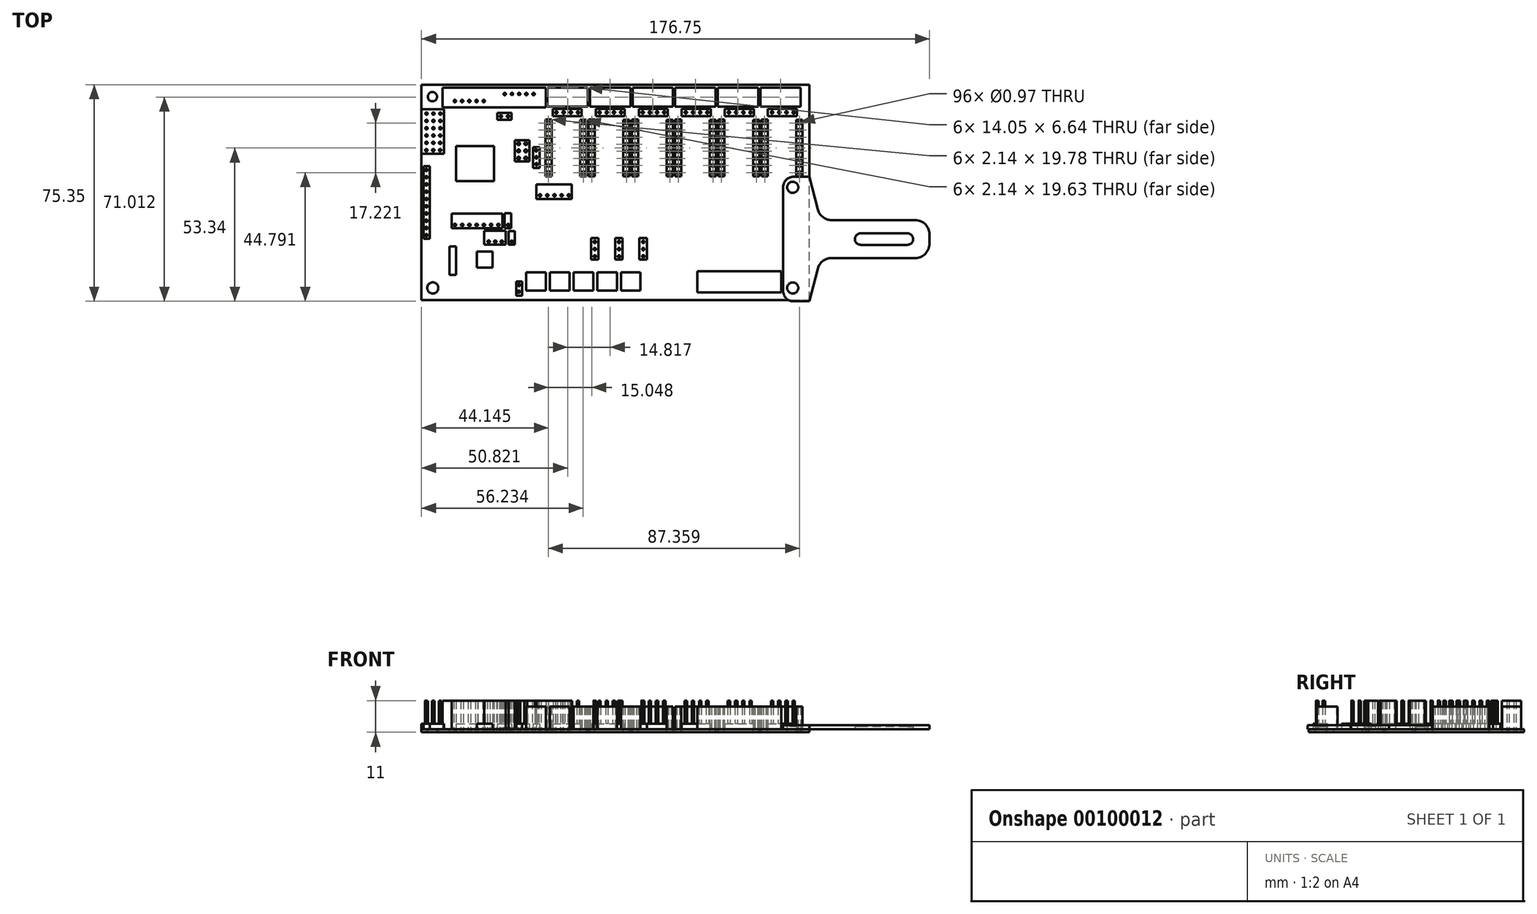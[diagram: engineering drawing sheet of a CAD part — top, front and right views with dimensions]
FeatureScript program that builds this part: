
annotation { "Feature Type Name" : "Feature", "Feature Type Description" : "" }
export const myFeature = defineFeature(function(context is Context, id is Id, definition is map)
    precondition{}
    {
        {
            var Q0;
            Q0=qCreatedBy(makeId("Top.planeOp"),FACE);
            var sketch = newSketch(context, id + "F0", { "sketchPlane" : qUnion([Q0])});
            skLineSegment(sketch, "E0", {"start": v(-38.75, 31.78) * mm, "end": v(-38.75, -41.43) * mm});
            skLineSegment(sketch, "E1", {"start": v(-38.75, -41.43) * mm, "end": v(96.25, -41.43) * mm});
            skLineSegment(sketch, "E2", {"start": v(96.25, -41.43) * mm, "end": v(96.25, 33.57) * mm});
            skLineSegment(sketch, "E3.bottom", {"start": v(-2.37, -31.77) * mm, "end": v(4.45, -31.77) * mm});
            skLineSegment(sketch, "E3.top", {"start": v(-2.37, -38.05) * mm, "end": v(4.45, -38.05) * mm});
            skLineSegment(sketch, "E3.left", {"start": v(-2.37, -31.77) * mm, "end": v(-2.37, -38.05) * mm});
            skLineSegment(sketch, "E3.right", {"start": v(4.45, -31.77) * mm, "end": v(4.45, -38.05) * mm});
            skLineSegment(sketch, "E4.1.0.0", {"start": v(12.7, -31.77) * mm, "end": v(12.7, -38.05) * mm});
            skLineSegment(sketch, "E4.1.0.1", {"start": v(5.88, -31.77) * mm, "end": v(12.7, -31.77) * mm});
            skLineSegment(sketch, "E4.1.0.2", {"start": v(5.88, -31.77) * mm, "end": v(5.88, -38.05) * mm});
            skLineSegment(sketch, "E4.1.0.3", {"start": v(5.88, -38.05) * mm, "end": v(12.7, -38.05) * mm});
            skLineSegment(sketch, "E4.2.0.0", {"start": v(20.95, -31.77) * mm, "end": v(20.95, -38.05) * mm});
            skLineSegment(sketch, "E4.2.0.1", {"start": v(14.13, -31.77) * mm, "end": v(20.95, -31.77) * mm});
            skLineSegment(sketch, "E4.2.0.2", {"start": v(14.13, -31.77) * mm, "end": v(14.13, -38.05) * mm});
            skLineSegment(sketch, "E4.2.0.3", {"start": v(14.13, -38.05) * mm, "end": v(20.95, -38.05) * mm});
            skLineSegment(sketch, "E4.3.0.0", {"start": v(29.2, -31.77) * mm, "end": v(29.2, -38.05) * mm});
            skLineSegment(sketch, "E4.3.0.1", {"start": v(22.38, -31.77) * mm, "end": v(29.2, -31.77) * mm});
            skLineSegment(sketch, "E4.3.0.2", {"start": v(22.38, -31.77) * mm, "end": v(22.38, -38.05) * mm});
            skLineSegment(sketch, "E4.3.0.3", {"start": v(22.38, -38.05) * mm, "end": v(29.2, -38.05) * mm});
            skLineSegment(sketch, "E4.4.0.0", {"start": v(37.45, -31.77) * mm, "end": v(37.45, -38.05) * mm});
            skLineSegment(sketch, "E4.4.0.1", {"start": v(30.63, -31.77) * mm, "end": v(37.45, -31.77) * mm});
            skLineSegment(sketch, "E4.4.0.2", {"start": v(30.63, -31.77) * mm, "end": v(30.63, -38.05) * mm});
            skLineSegment(sketch, "E4.4.0.3", {"start": v(30.63, -38.05) * mm, "end": v(37.45, -38.05) * mm});
            skLineSegment(sketch, "E4.direction1", {"start": v(-2.37, -38.05) * mm, "end": v(5.88, -38.05) * mm, "construction": true});
            skLineSegment(sketch, "E5", {"start": v(57.17, -31.32) * mm, "end": v(86.44, -31.32) * mm});
            skLineSegment(sketch, "E6", {"start": v(86.44, -31.32) * mm, "end": v(86.44, -38.69) * mm});
            skLineSegment(sketch, "E7", {"start": v(86.44, -38.69) * mm, "end": v(57.17, -38.69) * mm});
            skLineSegment(sketch, "E8", {"start": v(57.17, -38.69) * mm, "end": v(57.17, -31.32) * mm});
            skLineSegment(sketch, "E9.bottom", {"start": v(20.26, -19.76) * mm, "end": v(22.82, -19.76) * mm});
            skLineSegment(sketch, "E9.top", {"start": v(20.26, -27.24) * mm, "end": v(22.82, -27.24) * mm});
            skLineSegment(sketch, "E9.left", {"start": v(20.26, -19.76) * mm, "end": v(20.26, -27.24) * mm});
            skLineSegment(sketch, "E9.right", {"start": v(22.82, -19.76) * mm, "end": v(22.82, -27.24) * mm});
            skLineSegment(sketch, "E10.1.0.0", {"start": v(28.66, -19.76) * mm, "end": v(31.22, -19.76) * mm});
            skLineSegment(sketch, "E10.1.0.1", {"start": v(31.22, -19.76) * mm, "end": v(31.22, -27.24) * mm});
            skLineSegment(sketch, "E10.1.0.2", {"start": v(28.66, -19.76) * mm, "end": v(28.66, -27.24) * mm});
            skLineSegment(sketch, "E10.1.0.3", {"start": v(28.66, -27.24) * mm, "end": v(31.22, -27.24) * mm});
            skLineSegment(sketch, "E10.2.0.0", {"start": v(37.06, -19.76) * mm, "end": v(39.63, -19.76) * mm});
            skLineSegment(sketch, "E10.2.0.1", {"start": v(39.63, -19.76) * mm, "end": v(39.63, -27.24) * mm});
            skLineSegment(sketch, "E10.2.0.2", {"start": v(37.06, -19.76) * mm, "end": v(37.06, -27.24) * mm});
            skLineSegment(sketch, "E10.2.0.3", {"start": v(37.06, -27.24) * mm, "end": v(39.63, -27.24) * mm});
            skLineSegment(sketch, "E10.direction1", {"start": v(20.26, -27.24) * mm, "end": v(28.66, -27.24) * mm, "construction": true});
            skLineSegment(sketch, "E11.bottom", {"start": v(-28.27, -11.21) * mm, "end": v(-10.6, -11.21) * mm});
            skLineSegment(sketch, "E11.top", {"start": v(-28.27, -16.39) * mm, "end": v(-10.6, -16.39) * mm});
            skLineSegment(sketch, "E11.left", {"start": v(-28.27, -11.21) * mm, "end": v(-28.27, -16.39) * mm});
            skLineSegment(sketch, "E11.right", {"start": v(-10.6, -11.21) * mm, "end": v(-10.6, -16.39) * mm});
            skLineSegment(sketch, "E12.bottom", {"start": v(-17, -17.19) * mm, "end": v(-9.44, -17.19) * mm});
            skLineSegment(sketch, "E12.top", {"start": v(-17, -22.08) * mm, "end": v(-9.44, -22.08) * mm});
            skLineSegment(sketch, "E12.left", {"start": v(-17, -17.19) * mm, "end": v(-17, -22.08) * mm});
            skLineSegment(sketch, "E12.right", {"start": v(-9.44, -17.19) * mm, "end": v(-9.44, -22.08) * mm});
            skLineSegment(sketch, "E13.bottom", {"start": v(-8.45, -17.31) * mm, "end": v(-6.31, -17.31) * mm});
            skLineSegment(sketch, "E13.top", {"start": v(-8.45, -22) * mm, "end": v(-6.31, -22) * mm});
            skLineSegment(sketch, "E13.left", {"start": v(-8.45, -17.31) * mm, "end": v(-8.45, -22) * mm});
            skLineSegment(sketch, "E13.right", {"start": v(-6.31, -17.31) * mm, "end": v(-6.31, -22) * mm});
            skLineSegment(sketch, "E14.bottom", {"start": v(-5.85, -34.9) * mm, "end": v(-3.8, -34.9) * mm});
            skLineSegment(sketch, "E14.top", {"start": v(-5.85, -39.87) * mm, "end": v(-3.8, -39.87) * mm});
            skLineSegment(sketch, "E14.left", {"start": v(-5.85, -34.9) * mm, "end": v(-5.85, -39.87) * mm});
            skLineSegment(sketch, "E14.right", {"start": v(-3.8, -34.9) * mm, "end": v(-3.8, -39.87) * mm});
            skLineSegment(sketch, "E15.bottom", {"start": v(-29, -22.74) * mm, "end": v(-26.78, -22.74) * mm});
            skLineSegment(sketch, "E15.top", {"start": v(-29, -32.62) * mm, "end": v(-26.78, -32.62) * mm});
            skLineSegment(sketch, "E15.left", {"start": v(-29, -22.74) * mm, "end": v(-29, -32.62) * mm});
            skLineSegment(sketch, "E15.right", {"start": v(-26.78, -22.74) * mm, "end": v(-26.78, -32.62) * mm});
            skLineSegment(sketch, "E16.bottom", {"start": v(1.15, -1.07) * mm, "end": v(13.52, -1.07) * mm});
            skLineSegment(sketch, "E16.top", {"start": v(1.15, -6.2) * mm, "end": v(13.52, -6.2) * mm});
            skLineSegment(sketch, "E16.left", {"start": v(1.15, -1.07) * mm, "end": v(1.15, -6.2) * mm});
            skLineSegment(sketch, "E16.right", {"start": v(13.52, -1.07) * mm, "end": v(13.52, -6.2) * mm});
            skLineSegment(sketch, "E17.bottom", {"start": v(-38.08, 5.19) * mm, "end": v(-35.87, 5.19) * mm});
            skLineSegment(sketch, "E17.top", {"start": v(-38.08, -20.02) * mm, "end": v(-35.87, -20.02) * mm});
            skLineSegment(sketch, "E17.left", {"start": v(-38.08, 5.19) * mm, "end": v(-38.08, -20.02) * mm});
            skLineSegment(sketch, "E17.right", {"start": v(-35.87, 5.19) * mm, "end": v(-35.87, -20.02) * mm});
            skLineSegment(sketch, "E18.bottom", {"start": v(0.03, 11.83) * mm, "end": v(2.32, 11.83) * mm});
            skLineSegment(sketch, "E18.top", {"start": v(0.03, 4.65) * mm, "end": v(2.32, 4.65) * mm});
            skLineSegment(sketch, "E18.left", {"start": v(0.03, 11.83) * mm, "end": v(0.03, 4.65) * mm});
            skLineSegment(sketch, "E18.right", {"start": v(2.32, 11.83) * mm, "end": v(2.32, 4.65) * mm});
            skLineSegment(sketch, "E19.bottom", {"start": v(-12.42, 23.8) * mm, "end": v(-7.46, 23.8) * mm});
            skLineSegment(sketch, "E19.top", {"start": v(-12.42, 21.38) * mm, "end": v(-7.46, 21.38) * mm});
            skLineSegment(sketch, "E19.left", {"start": v(-12.42, 23.8) * mm, "end": v(-12.42, 21.38) * mm});
            skLineSegment(sketch, "E19.right", {"start": v(-7.46, 23.8) * mm, "end": v(-7.46, 21.38) * mm});
            skLineSegment(sketch, "E20.bottom", {"start": v(-26.74, 12.21) * mm, "end": v(-13.5, 12.21) * mm});
            skLineSegment(sketch, "E20.top", {"start": v(-26.74, 0.07) * mm, "end": v(-13.5, 0.07) * mm});
            skLineSegment(sketch, "E20.left", {"start": v(-26.74, 12.21) * mm, "end": v(-26.74, 0.07) * mm});
            skLineSegment(sketch, "E20.right", {"start": v(-13.5, 12.21) * mm, "end": v(-13.5, 0.07) * mm});
            skLineSegment(sketch, "E21.bottom", {"start": v(-38.75, 25.04) * mm, "end": v(-30.92, 25.04) * mm});
            skLineSegment(sketch, "E21.top", {"start": v(-38.75, 9.54) * mm, "end": v(-30.92, 9.54) * mm});
            skLineSegment(sketch, "E21.left", {"start": v(-38.75, 25.04) * mm, "end": v(-38.75, 9.54) * mm});
            skLineSegment(sketch, "E21.right", {"start": v(-30.92, 25.04) * mm, "end": v(-30.92, 9.54) * mm});
            skLineSegment(sketch, "E22", {"start": v(96.25, 33.57) * mm, "end": v(-38.75, 33.57) * mm});
            skLineSegment(sketch, "E23", {"start": v(-38.75, 33.57) * mm, "end": v(-38.75, 31.78) * mm});
            skLineSegment(sketch, "E24.bottom", {"start": v(-31.44, 32.53) * mm, "end": v(4.51, 32.53) * mm});
            skLineSegment(sketch, "E24.top", {"start": v(-31.44, 25.72) * mm, "end": v(4.51, 25.72) * mm});
            skLineSegment(sketch, "E24.left", {"start": v(-31.44, 32.53) * mm, "end": v(-31.44, 25.72) * mm});
            skLineSegment(sketch, "E24.right", {"start": v(4.51, 32.53) * mm, "end": v(4.51, 25.72) * mm});
            skLineSegment(sketch, "E25.bottom", {"start": v(5.04, 32.55) * mm, "end": v(19.1, 32.55) * mm});
            skLineSegment(sketch, "E25.top", {"start": v(5.04, 25.9) * mm, "end": v(19.1, 25.9) * mm});
            skLineSegment(sketch, "E25.left", {"start": v(5.04, 32.55) * mm, "end": v(5.04, 25.9) * mm});
            skLineSegment(sketch, "E25.right", {"start": v(19.1, 32.55) * mm, "end": v(19.1, 25.9) * mm});
            skLineSegment(sketch, "E26.1.0.0", {"start": v(33.91, 32.55) * mm, "end": v(33.91, 25.9) * mm});
            skLineSegment(sketch, "E26.1.0.1", {"start": v(19.86, 32.55) * mm, "end": v(33.91, 32.55) * mm});
            skLineSegment(sketch, "E26.1.0.2", {"start": v(19.86, 32.55) * mm, "end": v(19.86, 25.9) * mm});
            skLineSegment(sketch, "E26.1.0.3", {"start": v(19.86, 25.9) * mm, "end": v(33.91, 25.9) * mm});
            skLineSegment(sketch, "E26.2.0.0", {"start": v(48.73, 32.55) * mm, "end": v(48.73, 25.9) * mm});
            skLineSegment(sketch, "E26.2.0.1", {"start": v(34.68, 32.55) * mm, "end": v(48.73, 32.55) * mm});
            skLineSegment(sketch, "E26.2.0.2", {"start": v(34.68, 32.55) * mm, "end": v(34.68, 25.9) * mm});
            skLineSegment(sketch, "E26.2.0.3", {"start": v(34.68, 25.9) * mm, "end": v(48.73, 25.9) * mm});
            skLineSegment(sketch, "E26.3.0.0", {"start": v(63.55, 32.55) * mm, "end": v(63.55, 25.9) * mm});
            skLineSegment(sketch, "E26.3.0.1", {"start": v(49.5, 32.55) * mm, "end": v(63.55, 32.55) * mm});
            skLineSegment(sketch, "E26.3.0.2", {"start": v(49.5, 32.55) * mm, "end": v(49.5, 25.9) * mm});
            skLineSegment(sketch, "E26.3.0.3", {"start": v(49.5, 25.9) * mm, "end": v(63.55, 25.9) * mm});
            skLineSegment(sketch, "E26.4.0.0", {"start": v(78.36, 32.55) * mm, "end": v(78.36, 25.9) * mm});
            skLineSegment(sketch, "E26.4.0.1", {"start": v(64.31, 32.55) * mm, "end": v(78.36, 32.55) * mm});
            skLineSegment(sketch, "E26.4.0.2", {"start": v(64.31, 32.55) * mm, "end": v(64.31, 25.9) * mm});
            skLineSegment(sketch, "E26.4.0.3", {"start": v(64.31, 25.9) * mm, "end": v(78.36, 25.9) * mm});
            skLineSegment(sketch, "E26.5.0.0", {"start": v(93.18, 32.55) * mm, "end": v(93.18, 25.9) * mm});
            skLineSegment(sketch, "E26.5.0.1", {"start": v(79.13, 32.55) * mm, "end": v(93.18, 32.55) * mm});
            skLineSegment(sketch, "E26.5.0.2", {"start": v(79.13, 32.55) * mm, "end": v(79.13, 25.9) * mm});
            skLineSegment(sketch, "E26.5.0.3", {"start": v(79.13, 25.9) * mm, "end": v(93.18, 25.9) * mm});
            skLineSegment(sketch, "E26.direction1", {"start": v(5.04, 25.9) * mm, "end": v(19.86, 25.9) * mm, "construction": true});
            skLineSegment(sketch, "E27.bottom", {"start": v(4.33, 21.45) * mm, "end": v(6.46, 21.45) * mm});
            skLineSegment(sketch, "E27.top", {"start": v(4.33, 1.67) * mm, "end": v(6.46, 1.67) * mm});
            skLineSegment(sketch, "E27.left", {"start": v(4.33, 21.45) * mm, "end": v(4.33, 1.67) * mm});
            skLineSegment(sketch, "E27.right", {"start": v(6.46, 21.45) * mm, "end": v(6.46, 1.67) * mm});
            skLineSegment(sketch, "E28.bottom", {"start": v(16.41, 21.37) * mm, "end": v(18.55, 21.37) * mm});
            skLineSegment(sketch, "E28.top", {"start": v(16.41, 1.75) * mm, "end": v(18.55, 1.75) * mm});
            skLineSegment(sketch, "E28.left", {"start": v(16.41, 21.37) * mm, "end": v(16.41, 1.75) * mm});
            skLineSegment(sketch, "E28.right", {"start": v(18.55, 21.37) * mm, "end": v(18.55, 1.75) * mm});
            skLineSegment(sketch, "E29.1.0.0", {"start": v(19.37, 21.45) * mm, "end": v(21.51, 21.45) * mm});
            skLineSegment(sketch, "E29.1.0.1", {"start": v(21.51, 21.45) * mm, "end": v(21.51, 1.67) * mm});
            skLineSegment(sketch, "E29.1.0.2", {"start": v(19.37, 21.45) * mm, "end": v(19.37, 1.67) * mm});
            skLineSegment(sketch, "E29.1.0.3", {"start": v(19.37, 1.67) * mm, "end": v(21.51, 1.67) * mm});
            skLineSegment(sketch, "E29.1.0.4", {"start": v(31.46, 21.37) * mm, "end": v(31.46, 1.75) * mm});
            skLineSegment(sketch, "E29.1.0.5", {"start": v(31.46, 1.75) * mm, "end": v(33.6, 1.75) * mm});
            skLineSegment(sketch, "E29.1.0.6", {"start": v(33.6, 21.37) * mm, "end": v(33.6, 1.75) * mm});
            skLineSegment(sketch, "E29.1.0.7", {"start": v(31.46, 21.37) * mm, "end": v(33.6, 21.37) * mm});
            skLineSegment(sketch, "E29.2.0.0", {"start": v(34.42, 21.45) * mm, "end": v(36.56, 21.45) * mm});
            skLineSegment(sketch, "E29.2.0.1", {"start": v(36.56, 21.45) * mm, "end": v(36.56, 1.67) * mm});
            skLineSegment(sketch, "E29.2.0.2", {"start": v(34.42, 21.45) * mm, "end": v(34.42, 1.67) * mm});
            skLineSegment(sketch, "E29.2.0.3", {"start": v(34.42, 1.67) * mm, "end": v(36.56, 1.67) * mm});
            skLineSegment(sketch, "E29.2.0.4", {"start": v(46.51, 21.37) * mm, "end": v(46.51, 1.75) * mm});
            skLineSegment(sketch, "E29.2.0.5", {"start": v(46.51, 1.75) * mm, "end": v(48.65, 1.75) * mm});
            skLineSegment(sketch, "E29.2.0.6", {"start": v(48.65, 21.37) * mm, "end": v(48.65, 1.75) * mm});
            skLineSegment(sketch, "E29.2.0.7", {"start": v(46.51, 21.37) * mm, "end": v(48.65, 21.37) * mm});
            skLineSegment(sketch, "E29.3.0.0", {"start": v(49.47, 21.45) * mm, "end": v(51.6, 21.45) * mm});
            skLineSegment(sketch, "E29.3.0.1", {"start": v(51.6, 21.45) * mm, "end": v(51.6, 1.67) * mm});
            skLineSegment(sketch, "E29.3.0.2", {"start": v(49.47, 21.45) * mm, "end": v(49.47, 1.67) * mm});
            skLineSegment(sketch, "E29.3.0.3", {"start": v(49.47, 1.67) * mm, "end": v(51.6, 1.67) * mm});
            skLineSegment(sketch, "E29.3.0.4", {"start": v(61.56, 21.37) * mm, "end": v(61.56, 1.75) * mm});
            skLineSegment(sketch, "E29.3.0.5", {"start": v(61.56, 1.75) * mm, "end": v(63.7, 1.75) * mm});
            skLineSegment(sketch, "E29.3.0.6", {"start": v(63.7, 21.37) * mm, "end": v(63.7, 1.75) * mm});
            skLineSegment(sketch, "E29.3.0.7", {"start": v(61.56, 21.37) * mm, "end": v(63.7, 21.37) * mm});
            skLineSegment(sketch, "E29.4.0.0", {"start": v(64.52, 21.45) * mm, "end": v(66.66, 21.45) * mm});
            skLineSegment(sketch, "E29.4.0.1", {"start": v(66.66, 21.45) * mm, "end": v(66.66, 1.67) * mm});
            skLineSegment(sketch, "E29.4.0.2", {"start": v(64.52, 21.45) * mm, "end": v(64.52, 1.67) * mm});
            skLineSegment(sketch, "E29.4.0.3", {"start": v(64.52, 1.67) * mm, "end": v(66.66, 1.67) * mm});
            skLineSegment(sketch, "E29.4.0.4", {"start": v(76.6, 21.37) * mm, "end": v(76.6, 1.75) * mm});
            skLineSegment(sketch, "E29.4.0.5", {"start": v(76.6, 1.75) * mm, "end": v(78.75, 1.75) * mm});
            skLineSegment(sketch, "E29.4.0.6", {"start": v(78.75, 21.37) * mm, "end": v(78.75, 1.75) * mm});
            skLineSegment(sketch, "E29.4.0.7", {"start": v(76.6, 21.37) * mm, "end": v(78.75, 21.37) * mm});
            skLineSegment(sketch, "E29.5.0.0", {"start": v(79.57, 21.45) * mm, "end": v(81.7, 21.45) * mm});
            skLineSegment(sketch, "E29.5.0.1", {"start": v(81.7, 21.45) * mm, "end": v(81.7, 1.67) * mm});
            skLineSegment(sketch, "E29.5.0.2", {"start": v(79.57, 21.45) * mm, "end": v(79.57, 1.67) * mm});
            skLineSegment(sketch, "E29.5.0.3", {"start": v(79.57, 1.67) * mm, "end": v(81.7, 1.67) * mm});
            skLineSegment(sketch, "E29.5.0.4", {"start": v(91.66, 21.37) * mm, "end": v(91.66, 1.75) * mm});
            skLineSegment(sketch, "E29.5.0.5", {"start": v(91.66, 1.75) * mm, "end": v(93.8, 1.75) * mm});
            skLineSegment(sketch, "E29.5.0.6", {"start": v(93.8, 21.37) * mm, "end": v(93.8, 1.75) * mm});
            skLineSegment(sketch, "E29.5.0.7", {"start": v(91.66, 21.37) * mm, "end": v(93.8, 21.37) * mm});
            skLineSegment(sketch, "E30.bottom", {"start": v(-9.85, -11.19) * mm, "end": v(-7.56, -11.19) * mm});
            skLineSegment(sketch, "E30.top", {"start": v(-9.85, -16.36) * mm, "end": v(-7.56, -16.36) * mm});
            skLineSegment(sketch, "E30.left", {"start": v(-9.85, -11.19) * mm, "end": v(-9.85, -16.36) * mm});
            skLineSegment(sketch, "E30.right", {"start": v(-7.56, -11.19) * mm, "end": v(-7.56, -16.36) * mm});
            skLineSegment(sketch, "E31.bottom", {"start": v(6.88, 25.2) * mm, "end": v(16.96, 25.2) * mm});
            skLineSegment(sketch, "E31.top", {"start": v(6.88, 22.67) * mm, "end": v(16.96, 22.67) * mm});
            skLineSegment(sketch, "E31.left", {"start": v(6.88, 25.2) * mm, "end": v(6.88, 22.67) * mm});
            skLineSegment(sketch, "E31.right", {"start": v(16.96, 25.2) * mm, "end": v(16.96, 22.67) * mm});
            skLineSegment(sketch, "E32.1.0.0", {"start": v(21.85, 25.2) * mm, "end": v(21.85, 22.67) * mm});
            skLineSegment(sketch, "E32.1.0.1", {"start": v(21.85, 25.2) * mm, "end": v(31.93, 25.2) * mm});
            skLineSegment(sketch, "E32.1.0.2", {"start": v(31.93, 25.2) * mm, "end": v(31.93, 22.67) * mm});
            skLineSegment(sketch, "E32.1.0.3", {"start": v(21.85, 22.67) * mm, "end": v(31.93, 22.67) * mm});
            skLineSegment(sketch, "E32.2.0.0", {"start": v(36.82, 25.2) * mm, "end": v(36.82, 22.67) * mm});
            skLineSegment(sketch, "E32.2.0.1", {"start": v(36.82, 25.2) * mm, "end": v(46.9, 25.2) * mm});
            skLineSegment(sketch, "E32.2.0.2", {"start": v(46.9, 25.2) * mm, "end": v(46.9, 22.67) * mm});
            skLineSegment(sketch, "E32.2.0.3", {"start": v(36.82, 22.67) * mm, "end": v(46.9, 22.67) * mm});
            skLineSegment(sketch, "E32.3.0.0", {"start": v(51.79, 25.2) * mm, "end": v(51.79, 22.67) * mm});
            skLineSegment(sketch, "E32.3.0.1", {"start": v(51.79, 25.2) * mm, "end": v(61.87, 25.2) * mm});
            skLineSegment(sketch, "E32.3.0.2", {"start": v(61.87, 25.2) * mm, "end": v(61.87, 22.67) * mm});
            skLineSegment(sketch, "E32.3.0.3", {"start": v(51.79, 22.67) * mm, "end": v(61.87, 22.67) * mm});
            skLineSegment(sketch, "E32.4.0.0", {"start": v(66.76, 25.2) * mm, "end": v(66.76, 22.67) * mm});
            skLineSegment(sketch, "E32.4.0.1", {"start": v(66.76, 25.2) * mm, "end": v(76.84, 25.2) * mm});
            skLineSegment(sketch, "E32.4.0.2", {"start": v(76.84, 25.2) * mm, "end": v(76.84, 22.67) * mm});
            skLineSegment(sketch, "E32.4.0.3", {"start": v(66.76, 22.67) * mm, "end": v(76.84, 22.67) * mm});
            skLineSegment(sketch, "E32.5.0.0", {"start": v(81.73, 25.2) * mm, "end": v(81.73, 22.67) * mm});
            skLineSegment(sketch, "E32.5.0.1", {"start": v(81.73, 25.2) * mm, "end": v(91.8, 25.2) * mm});
            skLineSegment(sketch, "E32.5.0.2", {"start": v(91.8, 25.2) * mm, "end": v(91.8, 22.67) * mm});
            skLineSegment(sketch, "E32.5.0.3", {"start": v(81.73, 22.67) * mm, "end": v(91.8, 22.67) * mm});
            skLineSegment(sketch, "E32.direction1", {"start": v(6.88, 22.67) * mm, "end": v(21.85, 22.67) * mm, "construction": true});
            skPoint(sketch, "E33.endSnap0", {"position": v(-34.84, 9.54) * mm});
            skCircle(sketch, "E34", {"center": v(-34.97, 29.41) * mm, "radius": 1.62 * mm});
            skCircle(sketch, "E35", {"center": v(-34.84, -37.14) * mm, "radius": 1.95 * mm});
            skCircle(sketch, "E36", {"center": v(90.39, -37.15) * mm, "radius": 1.95 * mm});
            skCircle(sketch, "E37", {"center": v(90.39, -2.13) * mm, "radius": 1.95 * mm});
            skLineSegment(sketch, "E38", {"start": v(-13.47, 32.53) * mm, "end": v(-13.47, 25.72) * mm});
            skLineSegment(sketch, "E39", {"start": v(67.06, -31.32) * mm, "end": v(67.06, -38.69) * mm});
            skLineSegment(sketch, "E40", {"start": v(76.68, -31.32) * mm, "end": v(76.68, -38.69) * mm});
            skLineSegment(sketch, "E41.bottom", {"start": v(-19.55, -24.47) * mm, "end": v(-14.07, -24.47) * mm});
            skLineSegment(sketch, "E41.top", {"start": v(-19.55, -30.03) * mm, "end": v(-14.07, -30.03) * mm});
            skLineSegment(sketch, "E41.left", {"start": v(-19.55, -24.47) * mm, "end": v(-19.55, -30.03) * mm});
            skLineSegment(sketch, "E41.right", {"start": v(-14.07, -24.47) * mm, "end": v(-14.07, -30.03) * mm});
            skCircle(sketch, "E42", {"center": v(5.4, 20.23) * mm, "radius": 0.49 * mm});
            skCircle(sketch, "E43.1.0.0", {"center": v(5.4, 17.77) * mm, "radius": 0.49 * mm});
            skCircle(sketch, "E43.2.0.0", {"center": v(5.4, 15.31) * mm, "radius": 0.49 * mm});
            skCircle(sketch, "E43.3.0.0", {"center": v(5.42, 12.85) * mm, "radius": 0.49 * mm});
            skCircle(sketch, "E43.4.0.0", {"center": v(5.42, 10.4) * mm, "radius": 0.49 * mm});
            skCircle(sketch, "E43.5.0.0", {"center": v(5.43, 7.93) * mm, "radius": 0.49 * mm});
            skCircle(sketch, "E43.6.0.0", {"center": v(5.44, 5.47) * mm, "radius": 0.49 * mm});
            skCircle(sketch, "E43.7.0.0", {"center": v(5.45, 3.01) * mm, "radius": 0.49 * mm});
            skLineSegment(sketch, "E43.direction1", {"start": v(5.4, 20.23) * mm, "end": v(5.4, 17.77) * mm, "construction": true});
            skCircle(sketch, "E44.1.0.0", {"center": v(17.49, 20.23) * mm, "radius": 0.49 * mm});
            skCircle(sketch, "E44.1.0.1", {"center": v(17.5, 17.77) * mm, "radius": 0.49 * mm});
            skCircle(sketch, "E44.1.0.2", {"center": v(17.5, 15.31) * mm, "radius": 0.49 * mm});
            skCircle(sketch, "E44.1.0.3", {"center": v(17.5, 12.85) * mm, "radius": 0.49 * mm});
            skCircle(sketch, "E44.1.0.4", {"center": v(17.52, 10.4) * mm, "radius": 0.49 * mm});
            skCircle(sketch, "E44.1.0.5", {"center": v(17.52, 7.93) * mm, "radius": 0.49 * mm});
            skCircle(sketch, "E44.1.0.6", {"center": v(17.53, 5.47) * mm, "radius": 0.49 * mm});
            skCircle(sketch, "E44.1.0.7", {"center": v(17.54, 3.01) * mm, "radius": 0.49 * mm});
            skLineSegment(sketch, "E44.direction1", {"start": v(5.45, 3.01) * mm, "end": v(17.54, 3.01) * mm, "construction": true});
            skCircle(sketch, "E45.1.0.0", {"center": v(20.44, 20.23) * mm, "radius": 0.49 * mm});
            skCircle(sketch, "E45.1.0.1", {"center": v(20.45, 17.77) * mm, "radius": 0.49 * mm});
            skCircle(sketch, "E45.1.0.2", {"center": v(20.45, 15.31) * mm, "radius": 0.49 * mm});
            skCircle(sketch, "E45.1.0.3", {"center": v(20.46, 12.85) * mm, "radius": 0.49 * mm});
            skCircle(sketch, "E45.1.0.4", {"center": v(20.47, 10.4) * mm, "radius": 0.49 * mm});
            skCircle(sketch, "E45.1.0.5", {"center": v(20.48, 7.93) * mm, "radius": 0.49 * mm});
            skCircle(sketch, "E45.1.0.6", {"center": v(20.48, 5.47) * mm, "radius": 0.49 * mm});
            skCircle(sketch, "E45.1.0.7", {"center": v(20.5, 3.01) * mm, "radius": 0.49 * mm});
            skCircle(sketch, "E45.1.0.8", {"center": v(32.53, 20.23) * mm, "radius": 0.49 * mm});
            skCircle(sketch, "E45.1.0.9", {"center": v(32.54, 17.77) * mm, "radius": 0.49 * mm});
            skCircle(sketch, "E45.1.0.10", {"center": v(32.54, 15.31) * mm, "radius": 0.49 * mm});
            skCircle(sketch, "E45.1.0.11", {"center": v(32.55, 12.85) * mm, "radius": 0.49 * mm});
            skCircle(sketch, "E45.1.0.12", {"center": v(32.56, 10.4) * mm, "radius": 0.49 * mm});
            skCircle(sketch, "E45.1.0.13", {"center": v(32.57, 7.93) * mm, "radius": 0.49 * mm});
            skCircle(sketch, "E45.1.0.14", {"center": v(32.57, 5.47) * mm, "radius": 0.49 * mm});
            skCircle(sketch, "E45.1.0.15", {"center": v(32.58, 3.01) * mm, "radius": 0.49 * mm});
            skCircle(sketch, "E45.2.0.0", {"center": v(35.48, 20.23) * mm, "radius": 0.49 * mm});
            skCircle(sketch, "E45.2.0.1", {"center": v(35.49, 17.77) * mm, "radius": 0.49 * mm});
            skCircle(sketch, "E45.2.0.2", {"center": v(35.5, 15.31) * mm, "radius": 0.49 * mm});
            skCircle(sketch, "E45.2.0.3", {"center": v(35.5, 12.85) * mm, "radius": 0.49 * mm});
            skCircle(sketch, "E45.2.0.4", {"center": v(35.51, 10.4) * mm, "radius": 0.49 * mm});
            skCircle(sketch, "E45.2.0.5", {"center": v(35.52, 7.93) * mm, "radius": 0.49 * mm});
            skCircle(sketch, "E45.2.0.6", {"center": v(35.53, 5.47) * mm, "radius": 0.49 * mm});
            skCircle(sketch, "E45.2.0.7", {"center": v(35.53, 3.01) * mm, "radius": 0.49 * mm});
            skCircle(sketch, "E45.2.0.8", {"center": v(47.57, 20.23) * mm, "radius": 0.49 * mm});
            skCircle(sketch, "E45.2.0.9", {"center": v(47.58, 17.77) * mm, "radius": 0.49 * mm});
            skCircle(sketch, "E45.2.0.10", {"center": v(47.59, 15.31) * mm, "radius": 0.49 * mm});
            skCircle(sketch, "E45.2.0.11", {"center": v(47.6, 12.85) * mm, "radius": 0.49 * mm});
            skCircle(sketch, "E45.2.0.12", {"center": v(47.6, 10.4) * mm, "radius": 0.49 * mm});
            skCircle(sketch, "E45.2.0.13", {"center": v(47.6, 7.93) * mm, "radius": 0.49 * mm});
            skCircle(sketch, "E45.2.0.14", {"center": v(47.62, 5.47) * mm, "radius": 0.49 * mm});
            skCircle(sketch, "E45.2.0.15", {"center": v(47.62, 3.01) * mm, "radius": 0.49 * mm});
            skCircle(sketch, "E45.3.0.0", {"center": v(50.52, 20.23) * mm, "radius": 0.49 * mm});
            skCircle(sketch, "E45.3.0.1", {"center": v(50.53, 17.77) * mm, "radius": 0.49 * mm});
            skCircle(sketch, "E45.3.0.2", {"center": v(50.54, 15.31) * mm, "radius": 0.49 * mm});
            skCircle(sketch, "E45.3.0.3", {"center": v(50.55, 12.85) * mm, "radius": 0.49 * mm});
            skCircle(sketch, "E45.3.0.4", {"center": v(50.55, 10.4) * mm, "radius": 0.49 * mm});
            skCircle(sketch, "E45.3.0.5", {"center": v(50.56, 7.93) * mm, "radius": 0.49 * mm});
            skCircle(sketch, "E45.3.0.6", {"center": v(50.57, 5.47) * mm, "radius": 0.49 * mm});
            skCircle(sketch, "E45.3.0.7", {"center": v(50.58, 3.01) * mm, "radius": 0.49 * mm});
            skCircle(sketch, "E45.3.0.8", {"center": v(62.62, 20.23) * mm, "radius": 0.49 * mm});
            skCircle(sketch, "E45.3.0.9", {"center": v(62.62, 17.77) * mm, "radius": 0.49 * mm});
            skCircle(sketch, "E45.3.0.10", {"center": v(62.63, 15.31) * mm, "radius": 0.49 * mm});
            skCircle(sketch, "E45.3.0.11", {"center": v(62.64, 12.85) * mm, "radius": 0.49 * mm});
            skCircle(sketch, "E45.3.0.12", {"center": v(62.65, 10.4) * mm, "radius": 0.49 * mm});
            skCircle(sketch, "E45.3.0.13", {"center": v(62.65, 7.93) * mm, "radius": 0.49 * mm});
            skCircle(sketch, "E45.3.0.14", {"center": v(62.66, 5.47) * mm, "radius": 0.49 * mm});
            skCircle(sketch, "E45.3.0.15", {"center": v(62.67, 3.01) * mm, "radius": 0.49 * mm});
            skCircle(sketch, "E45.4.0.0", {"center": v(65.57, 20.23) * mm, "radius": 0.49 * mm});
            skCircle(sketch, "E45.4.0.1", {"center": v(65.57, 17.77) * mm, "radius": 0.49 * mm});
            skCircle(sketch, "E45.4.0.2", {"center": v(65.58, 15.31) * mm, "radius": 0.49 * mm});
            skCircle(sketch, "E45.4.0.3", {"center": v(65.59, 12.85) * mm, "radius": 0.49 * mm});
            skCircle(sketch, "E45.4.0.4", {"center": v(65.6, 10.4) * mm, "radius": 0.49 * mm});
            skCircle(sketch, "E45.4.0.5", {"center": v(65.6, 7.93) * mm, "radius": 0.49 * mm});
            skCircle(sketch, "E45.4.0.6", {"center": v(65.61, 5.47) * mm, "radius": 0.49 * mm});
            skCircle(sketch, "E45.4.0.7", {"center": v(65.62, 3.01) * mm, "radius": 0.49 * mm});
            skCircle(sketch, "E45.4.0.8", {"center": v(77.66, 20.23) * mm, "radius": 0.49 * mm});
            skCircle(sketch, "E45.4.0.9", {"center": v(77.67, 17.77) * mm, "radius": 0.49 * mm});
            skCircle(sketch, "E45.4.0.10", {"center": v(77.67, 15.31) * mm, "radius": 0.49 * mm});
            skCircle(sketch, "E45.4.0.11", {"center": v(77.68, 12.85) * mm, "radius": 0.49 * mm});
            skCircle(sketch, "E45.4.0.12", {"center": v(77.69, 10.4) * mm, "radius": 0.49 * mm});
            skCircle(sketch, "E45.4.0.13", {"center": v(77.7, 7.93) * mm, "radius": 0.49 * mm});
            skCircle(sketch, "E45.4.0.14", {"center": v(77.7, 5.47) * mm, "radius": 0.49 * mm});
            skCircle(sketch, "E45.4.0.15", {"center": v(77.71, 3.01) * mm, "radius": 0.49 * mm});
            skCircle(sketch, "E45.5.0.0", {"center": v(80.61, 20.23) * mm, "radius": 0.49 * mm});
            skCircle(sketch, "E45.5.0.1", {"center": v(80.62, 17.77) * mm, "radius": 0.49 * mm});
            skCircle(sketch, "E45.5.0.2", {"center": v(80.63, 15.31) * mm, "radius": 0.49 * mm});
            skCircle(sketch, "E45.5.0.3", {"center": v(80.63, 12.85) * mm, "radius": 0.49 * mm});
            skCircle(sketch, "E45.5.0.4", {"center": v(80.64, 10.4) * mm, "radius": 0.49 * mm});
            skCircle(sketch, "E45.5.0.5", {"center": v(80.65, 7.93) * mm, "radius": 0.49 * mm});
            skCircle(sketch, "E45.5.0.6", {"center": v(80.65, 5.47) * mm, "radius": 0.49 * mm});
            skCircle(sketch, "E45.5.0.7", {"center": v(80.66, 3.01) * mm, "radius": 0.49 * mm});
            skCircle(sketch, "E45.5.0.8", {"center": v(92.7, 20.23) * mm, "radius": 0.49 * mm});
            skCircle(sketch, "E45.5.0.9", {"center": v(92.7, 17.77) * mm, "radius": 0.49 * mm});
            skCircle(sketch, "E45.5.0.10", {"center": v(92.72, 15.31) * mm, "radius": 0.49 * mm});
            skCircle(sketch, "E45.5.0.11", {"center": v(92.72, 12.85) * mm, "radius": 0.49 * mm});
            skCircle(sketch, "E45.5.0.12", {"center": v(92.73, 10.4) * mm, "radius": 0.49 * mm});
            skCircle(sketch, "E45.5.0.13", {"center": v(92.74, 7.93) * mm, "radius": 0.49 * mm});
            skCircle(sketch, "E45.5.0.14", {"center": v(92.75, 5.47) * mm, "radius": 0.49 * mm});
            skCircle(sketch, "E45.5.0.15", {"center": v(92.75, 3.01) * mm, "radius": 0.49 * mm});
            skLineSegment(sketch, "E45.direction1", {"start": v(5.45, 3.01) * mm, "end": v(20.5, 3.01) * mm, "construction": true});
            skLineSegment(sketch, "E46", {"start": v(-37, 25.04) * mm, "end": v(-37, 9.54) * mm, "construction": true});
            skCircle(sketch, "E47", {"center": v(-37, 23.54) * mm, "radius": 0.42 * mm});
            skCircle(sketch, "E48.1.0.0", {"center": v(-37.02, 21) * mm, "radius": 0.42 * mm});
            skCircle(sketch, "E48.2.0.0", {"center": v(-37.03, 18.45) * mm, "radius": 0.42 * mm});
            skCircle(sketch, "E48.3.0.0", {"center": v(-37.05, 15.9) * mm, "radius": 0.42 * mm});
            skCircle(sketch, "E48.4.0.0", {"center": v(-37.06, 13.35) * mm, "radius": 0.42 * mm});
            skCircle(sketch, "E48.5.0.0", {"center": v(-37.08, 10.8) * mm, "radius": 0.42 * mm});
            skLineSegment(sketch, "E48.direction1", {"start": v(-37, 23.54) * mm, "end": v(-37.02, 21) * mm, "construction": true});
            skCircle(sketch, "E49.1.0.0", {"center": v(-34.6, 23.54) * mm, "radius": 0.42 * mm});
            skCircle(sketch, "E49.1.0.1", {"center": v(-34.62, 21) * mm, "radius": 0.42 * mm});
            skCircle(sketch, "E49.1.0.2", {"center": v(-34.64, 18.45) * mm, "radius": 0.42 * mm});
            skCircle(sketch, "E49.1.0.3", {"center": v(-34.65, 15.9) * mm, "radius": 0.42 * mm});
            skCircle(sketch, "E49.1.0.4", {"center": v(-34.67, 13.35) * mm, "radius": 0.42 * mm});
            skCircle(sketch, "E49.1.0.5", {"center": v(-34.68, 10.8) * mm, "radius": 0.42 * mm});
            skCircle(sketch, "E49.2.0.0", {"center": v(-32.21, 23.54) * mm, "radius": 0.42 * mm});
            skCircle(sketch, "E49.2.0.1", {"center": v(-32.23, 21) * mm, "radius": 0.42 * mm});
            skCircle(sketch, "E49.2.0.2", {"center": v(-32.24, 18.45) * mm, "radius": 0.42 * mm});
            skCircle(sketch, "E49.2.0.3", {"center": v(-32.26, 15.9) * mm, "radius": 0.42 * mm});
            skCircle(sketch, "E49.2.0.4", {"center": v(-32.27, 13.35) * mm, "radius": 0.42 * mm});
            skCircle(sketch, "E49.2.0.5", {"center": v(-32.29, 10.8) * mm, "radius": 0.42 * mm});
            skLineSegment(sketch, "E49.direction1", {"start": v(-37, 23.54) * mm, "end": v(-34.6, 23.54) * mm, "construction": true});
            skLineSegment(sketch, "E50", {"start": v(-28.27, -13.8) * mm, "end": v(-2.72, -13.8) * mm, "construction": true});
            skPoint(sketch, "E50.endSnap0", {"position": v(-10.6, -13.8) * mm});
            skCircle(sketch, "E51", {"center": v(-8.61, -12.33) * mm, "radius": 0.42 * mm});
            skCircle(sketch, "E52.MirrorC", {"center": v(-8.61, -15.27) * mm, "radius": 0.42 * mm});
            skCircle(sketch, "E53", {"center": v(-27.16, -12.4) * mm, "radius": 0.42 * mm});
            skCircle(sketch, "E54.MirrorC", {"center": v(-27.16, -15.2) * mm, "radius": 0.42 * mm});
            skCircle(sketch, "E55.1.0.0", {"center": v(-24.63, -12.4) * mm, "radius": 0.42 * mm});
            skCircle(sketch, "E55.2.0.0", {"center": v(-22.1, -12.4) * mm, "radius": 0.42 * mm});
            skCircle(sketch, "E55.3.0.0", {"center": v(-19.58, -12.4) * mm, "radius": 0.42 * mm});
            skCircle(sketch, "E55.4.0.0", {"center": v(-17.05, -12.4) * mm, "radius": 0.42 * mm});
            skCircle(sketch, "E55.5.0.0", {"center": v(-14.53, -12.4) * mm, "radius": 0.42 * mm});
            skCircle(sketch, "E55.6.0.0", {"center": v(-12, -12.4) * mm, "radius": 0.42 * mm});
            skLineSegment(sketch, "E55.direction1", {"start": v(-27.16, -12.4) * mm, "end": v(-24.63, -12.4) * mm, "construction": true});
            skCircle(sketch, "E56.MirrorC", {"center": v(-24.63, -15.2) * mm, "radius": 0.42 * mm});
            skCircle(sketch, "E57.MirrorC", {"center": v(-22.1, -15.2) * mm, "radius": 0.42 * mm});
            skCircle(sketch, "E58.MirrorC", {"center": v(-17.05, -15.2) * mm, "radius": 0.42 * mm});
            skCircle(sketch, "E59.MirrorC", {"center": v(-14.53, -15.2) * mm, "radius": 0.42 * mm});
            skCircle(sketch, "E60.MirrorC", {"center": v(-19.58, -15.2) * mm, "radius": 0.42 * mm});
            skCircle(sketch, "E61.MirrorC", {"center": v(-12, -15.2) * mm, "radius": 0.42 * mm});
            skLineSegment(sketch, "E62", {"start": v(-17, -19.63) * mm, "end": v(-3.44, -19.66) * mm, "construction": true});
            skPoint(sketch, "E62.endSnap0", {"position": v(-6.31, -19.66) * mm});
            skCircle(sketch, "E63", {"center": v(-15.38, -18.26) * mm, "radius": 0.42 * mm});
            skCircle(sketch, "E64.1.0.0", {"center": v(-13.1, -18.26) * mm, "radius": 0.42 * mm});
            skCircle(sketch, "E64.2.0.0", {"center": v(-10.8, -18.26) * mm, "radius": 0.42 * mm});
            skLineSegment(sketch, "E64.direction1", {"start": v(-15.38, -18.26) * mm, "end": v(-13.1, -18.26) * mm, "construction": true});
            skCircle(sketch, "E65.MirrorC", {"center": v(-10.81, -21.03) * mm, "radius": 0.42 * mm});
            skCircle(sketch, "E66.MirrorC", {"center": v(-13.1, -21.02) * mm, "radius": 0.42 * mm});
            skLineSegment(sketch, "E67.MirrorCS", {"start": v(-15.39, -21.01) * mm, "end": v(-13.1, -21.02) * mm, "construction": true});
            skCircle(sketch, "E68.MirrorC", {"center": v(-15.39, -21.01) * mm, "radius": 0.42 * mm});
            skCircle(sketch, "E69", {"center": v(-7.34, -18.2) * mm, "radius": 0.42 * mm});
            skCircle(sketch, "E70.MirrorC", {"center": v(-7.35, -21.09) * mm, "radius": 0.42 * mm});
            skCircle(sketch, "E71", {"center": v(-37.06, 3.93) * mm, "radius": 0.42 * mm});
            skCircle(sketch, "E72.1.0.0", {"center": v(-37.06, 1.4) * mm, "radius": 0.42 * mm});
            skCircle(sketch, "E72.2.0.0", {"center": v(-37.06, -1.13) * mm, "radius": 0.42 * mm});
            skCircle(sketch, "E72.3.0.0", {"center": v(-37.06, -3.65) * mm, "radius": 0.42 * mm});
            skCircle(sketch, "E72.4.0.0", {"center": v(-37.06, -6.18) * mm, "radius": 0.42 * mm});
            skCircle(sketch, "E72.5.0.0", {"center": v(-37.06, -8.7) * mm, "radius": 0.42 * mm});
            skCircle(sketch, "E72.6.0.0", {"center": v(-37.06, -11.24) * mm, "radius": 0.42 * mm});
            skCircle(sketch, "E72.7.0.0", {"center": v(-37.06, -13.76) * mm, "radius": 0.42 * mm});
            skCircle(sketch, "E72.8.0.0", {"center": v(-37.06, -16.3) * mm, "radius": 0.42 * mm});
            skCircle(sketch, "E72.9.0.0", {"center": v(-37.06, -18.82) * mm, "radius": 0.42 * mm});
            skLineSegment(sketch, "E72.direction1", {"start": v(-37.06, 3.93) * mm, "end": v(-37.06, 1.4) * mm, "construction": true});
            skCircle(sketch, "E73", {"center": v(21.54, -21.11) * mm, "radius": 0.42 * mm});
            skPoint(sketch, "E73.centerSnap0", {"position": v(21.54, -19.76) * mm});
            skCircle(sketch, "E74.1.0.0", {"center": v(29.97, -21.11) * mm, "radius": 0.42 * mm});
            skCircle(sketch, "E74.2.0.0", {"center": v(38.4, -21.11) * mm, "radius": 0.42 * mm});
            skLineSegment(sketch, "E74.direction1", {"start": v(21.54, -21.11) * mm, "end": v(29.97, -21.11) * mm, "construction": true});
            skCircle(sketch, "E75.1.0.0", {"center": v(21.54, -23.64) * mm, "radius": 0.42 * mm});
            skCircle(sketch, "E75.1.0.1", {"center": v(29.97, -23.64) * mm, "radius": 0.42 * mm});
            skCircle(sketch, "E75.1.0.2", {"center": v(38.4, -23.64) * mm, "radius": 0.42 * mm});
            skCircle(sketch, "E75.2.0.0", {"center": v(21.54, -26.16) * mm, "radius": 0.42 * mm});
            skCircle(sketch, "E75.2.0.1", {"center": v(29.97, -26.16) * mm, "radius": 0.42 * mm});
            skCircle(sketch, "E75.2.0.2", {"center": v(38.4, -26.16) * mm, "radius": 0.42 * mm});
            skLineSegment(sketch, "E75.direction1", {"start": v(21.54, -21.11) * mm, "end": v(21.54, -23.64) * mm, "construction": true});
            skCircle(sketch, "E76", {"center": v(-27.16, 30.35) * mm, "radius": 0.42 * mm});
            skLineSegment(sketch, "E77", {"start": v(-31.44, 29.13) * mm, "end": v(4.51, 29.13) * mm, "construction": true});
            skCircle(sketch, "E78.MirrorC", {"center": v(-27.16, 27.9) * mm, "radius": 0.42 * mm});
            skCircle(sketch, "E79.1.0.0", {"center": v(-24.65, 30.35) * mm, "radius": 0.42 * mm});
            skCircle(sketch, "E79.1.0.1", {"center": v(-24.65, 27.9) * mm, "radius": 0.42 * mm});
            skCircle(sketch, "E79.2.0.0", {"center": v(-22.14, 30.35) * mm, "radius": 0.42 * mm});
            skCircle(sketch, "E79.2.0.1", {"center": v(-22.14, 27.9) * mm, "radius": 0.42 * mm});
            skCircle(sketch, "E79.3.0.0", {"center": v(-19.63, 30.35) * mm, "radius": 0.42 * mm});
            skCircle(sketch, "E79.3.0.1", {"center": v(-19.63, 27.9) * mm, "radius": 0.42 * mm});
            skCircle(sketch, "E79.4.0.0", {"center": v(-17.11, 30.35) * mm, "radius": 0.42 * mm});
            skCircle(sketch, "E79.4.0.1", {"center": v(-17.11, 27.9) * mm, "radius": 0.42 * mm});
            skLineSegment(sketch, "E79.direction1", {"start": v(-27.16, 30.35) * mm, "end": v(-24.65, 30.35) * mm, "construction": true});
            skCircle(sketch, "E80.MirrorC", {"center": v(-9.82, 30.35) * mm, "radius": 0.42 * mm});
            skCircle(sketch, "E81.MirrorC", {"center": v(-9.82, 27.9) * mm, "radius": 0.42 * mm});
            skCircle(sketch, "E82.MirrorC", {"center": v(-7.3, 30.35) * mm, "radius": 0.42 * mm});
            skCircle(sketch, "E83.MirrorC", {"center": v(-7.3, 27.9) * mm, "radius": 0.42 * mm});
            skCircle(sketch, "E84.MirrorC", {"center": v(-4.8, 30.35) * mm, "radius": 0.42 * mm});
            skCircle(sketch, "E85.MirrorC", {"center": v(-4.8, 27.9) * mm, "radius": 0.42 * mm});
            skCircle(sketch, "E86.MirrorC", {"center": v(-2.28, 30.35) * mm, "radius": 0.42 * mm});
            skCircle(sketch, "E87.MirrorC", {"center": v(-2.28, 27.9) * mm, "radius": 0.42 * mm});
            skCircle(sketch, "E88.MirrorC", {"center": v(0.23, 30.35) * mm, "radius": 0.42 * mm});
            skCircle(sketch, "E89.MirrorC", {"center": v(0.23, 27.9) * mm, "radius": 0.42 * mm});
            skCircle(sketch, "E90", {"center": v(1.15, 10.75) * mm, "radius": 0.42 * mm});
            skCircle(sketch, "E91.1.0.0", {"center": v(1.2, 8.33) * mm, "radius": 0.42 * mm});
            skCircle(sketch, "E91.2.0.0", {"center": v(1.25, 5.9) * mm, "radius": 0.42 * mm});
            skLineSegment(sketch, "E91.direction1", {"start": v(1.15, 10.75) * mm, "end": v(1.2, 8.33) * mm, "construction": true});
            skLineSegment(sketch, "E92", {"start": v(1.15, -3.63) * mm, "end": v(13.52, -3.63) * mm, "construction": true});
            skCircle(sketch, "E93", {"center": v(2.47, -2.37) * mm, "radius": 0.42 * mm});
            skCircle(sketch, "E94.1.0.0", {"center": v(4.98, -2.37) * mm, "radius": 0.42 * mm});
            skCircle(sketch, "E94.2.0.0", {"center": v(7.5, -2.37) * mm, "radius": 0.42 * mm});
            skCircle(sketch, "E94.3.0.0", {"center": v(10, -2.37) * mm, "radius": 0.42 * mm});
            skCircle(sketch, "E94.4.0.0", {"center": v(12.51, -2.37) * mm, "radius": 0.42 * mm});
            skLineSegment(sketch, "E94.direction1", {"start": v(2.47, -2.37) * mm, "end": v(4.98, -2.37) * mm, "construction": true});
            skCircle(sketch, "E95.MirrorC", {"center": v(12.51, -4.9) * mm, "radius": 0.42 * mm});
            skCircle(sketch, "E96.MirrorC", {"center": v(10, -4.9) * mm, "radius": 0.42 * mm});
            skCircle(sketch, "E97.MirrorC", {"center": v(7.5, -4.9) * mm, "radius": 0.42 * mm});
            skCircle(sketch, "E98.MirrorC", {"center": v(4.98, -4.9) * mm, "radius": 0.42 * mm});
            skCircle(sketch, "E99.MirrorC", {"center": v(2.47, -4.9) * mm, "radius": 0.42 * mm});
            skLineSegment(sketch, "E100", {"start": v(-12.42, 22.59) * mm, "end": v(-7.46, 22.59) * mm, "construction": true});
            skCircle(sketch, "E101", {"center": v(-11.13, 22.58) * mm, "radius": 0.42 * mm});
            skCircle(sketch, "E102", {"center": v(-8.66, 22.59) * mm, "radius": 0.42 * mm});
            skCircle(sketch, "E103", {"center": v(8.17, 23.95) * mm, "radius": 0.42 * mm});
            skCircle(sketch, "E104.1.0.0", {"center": v(10.67, 23.95) * mm, "radius": 0.42 * mm});
            skCircle(sketch, "E104.2.0.0", {"center": v(13.18, 23.95) * mm, "radius": 0.42 * mm});
            skCircle(sketch, "E104.3.0.0", {"center": v(15.69, 23.95) * mm, "radius": 0.42 * mm});
            skLineSegment(sketch, "E104.direction1", {"start": v(8.17, 23.95) * mm, "end": v(10.67, 23.95) * mm, "construction": true});
            skCircle(sketch, "E105.1.0.0", {"center": v(23.18, 23.95) * mm, "radius": 0.42 * mm});
            skCircle(sketch, "E105.1.0.1", {"center": v(25.68, 23.95) * mm, "radius": 0.42 * mm});
            skCircle(sketch, "E105.1.0.2", {"center": v(28.19, 23.95) * mm, "radius": 0.42 * mm});
            skCircle(sketch, "E105.1.0.3", {"center": v(30.7, 23.95) * mm, "radius": 0.42 * mm});
            skCircle(sketch, "E105.2.0.0", {"center": v(38.18, 23.95) * mm, "radius": 0.42 * mm});
            skCircle(sketch, "E105.2.0.1", {"center": v(40.7, 23.95) * mm, "radius": 0.42 * mm});
            skCircle(sketch, "E105.2.0.2", {"center": v(43.2, 23.95) * mm, "radius": 0.42 * mm});
            skCircle(sketch, "E105.2.0.3", {"center": v(45.7, 23.95) * mm, "radius": 0.42 * mm});
            skCircle(sketch, "E105.3.0.0", {"center": v(53.2, 23.95) * mm, "radius": 0.42 * mm});
            skCircle(sketch, "E105.3.0.1", {"center": v(55.7, 23.95) * mm, "radius": 0.42 * mm});
            skCircle(sketch, "E105.3.0.2", {"center": v(58.2, 23.95) * mm, "radius": 0.42 * mm});
            skCircle(sketch, "E105.3.0.3", {"center": v(60.71, 23.95) * mm, "radius": 0.42 * mm});
            skCircle(sketch, "E105.4.0.0", {"center": v(68.2, 23.95) * mm, "radius": 0.42 * mm});
            skCircle(sketch, "E105.4.0.1", {"center": v(70.7, 23.95) * mm, "radius": 0.42 * mm});
            skCircle(sketch, "E105.4.0.2", {"center": v(73.21, 23.95) * mm, "radius": 0.42 * mm});
            skCircle(sketch, "E105.4.0.3", {"center": v(75.72, 23.95) * mm, "radius": 0.42 * mm});
            skCircle(sketch, "E105.5.0.0", {"center": v(83.21, 23.95) * mm, "radius": 0.42 * mm});
            skCircle(sketch, "E105.5.0.1", {"center": v(85.72, 23.95) * mm, "radius": 0.42 * mm});
            skCircle(sketch, "E105.5.0.2", {"center": v(88.22, 23.95) * mm, "radius": 0.42 * mm});
            skCircle(sketch, "E105.5.0.3", {"center": v(90.73, 23.95) * mm, "radius": 0.42 * mm});
            skLineSegment(sketch, "E105.direction1", {"start": v(8.17, 23.95) * mm, "end": v(23.18, 23.95) * mm, "construction": true});
            skCircle(sketch, "E106", {"center": v(-4.86, -36.13) * mm, "radius": 0.42 * mm});
            skLineSegment(sketch, "E107", {"start": v(-4.86, -36.13) * mm, "end": v(-4.86, -38.45) * mm, "construction": true});
            skCircle(sketch, "E108", {"center": v(-4.86, -38.45) * mm, "radius": 0.42 * mm});
            skLineSegment(sketch, "E109.bottom", {"start": v(-6.27, 14.21) * mm, "end": v(-1.2, 14.21) * mm});
            skLineSegment(sketch, "E109.top", {"start": v(-6.27, 6.85) * mm, "end": v(-1.2, 6.85) * mm});
            skLineSegment(sketch, "E109.left", {"start": v(-6.27, 14.21) * mm, "end": v(-6.27, 6.85) * mm});
            skLineSegment(sketch, "E109.right", {"start": v(-1.2, 14.21) * mm, "end": v(-1.2, 6.85) * mm});
            skCircle(sketch, "E110", {"center": v(-4.97, 13.06) * mm, "radius": 0.5 * mm});
            skCircle(sketch, "E111.1.0.0", {"center": v(-4.97, 10.55) * mm, "radius": 0.5 * mm});
            skCircle(sketch, "E111.2.0.0", {"center": v(-4.97, 8.03) * mm, "radius": 0.5 * mm});
            skLineSegment(sketch, "E111.direction1", {"start": v(-4.97, 13.06) * mm, "end": v(-4.97, 10.55) * mm, "construction": true});
            skCircle(sketch, "E112.1.0.0", {"center": v(-2.48, 13.06) * mm, "radius": 0.5 * mm});
            skCircle(sketch, "E112.1.0.1", {"center": v(-2.48, 10.55) * mm, "radius": 0.5 * mm});
            skCircle(sketch, "E112.1.0.2", {"center": v(-2.48, 8.03) * mm, "radius": 0.5 * mm});
            skLineSegment(sketch, "E112.direction1", {"start": v(-4.97, 13.06) * mm, "end": v(-2.48, 13.06) * mm, "construction": true});
            skSolve(sketch);
        }
        {
            var Q0;
            Q0=makeQuery(id+"F0.imprint","IMPRINT",FACE,{"disambiguationData":[TD([[makeQuery(id+"F0.imprint","IMPRINT",EDGE,{"derivedFrom":sQuery(id+"F0.wireOp",EDGE,"E27.bottom")}),-1.0]])]});
            var Q1;
            Q1=makeQuery(id+"F0.imprint","IMPRINT",FACE,{"disambiguationData":[TD([[makeQuery(id+"F0.imprint","IMPRINT",EDGE,{"derivedFrom":sQuery(id+"F0.wireOp",EDGE,"E28.bottom")}),-1.0]])]});
            var Q2;
            Q2=makeQuery(id+"F0.imprint","IMPRINT",FACE,{"disambiguationData":[TD([[makeQuery(id+"F0.imprint","IMPRINT",EDGE,{"derivedFrom":sQuery(id+"F0.wireOp",EDGE,"E29.1.0.0")}),-1.0]])]});
            var Q3;
            Q3=makeQuery(id+"F0.imprint","IMPRINT",FACE,{"disambiguationData":[TD([[makeQuery(id+"F0.imprint","IMPRINT",EDGE,{"derivedFrom":sQuery(id+"F0.wireOp",EDGE,"E29.1.0.4")}),1.0]])]});
            var Q4;
            Q4=makeQuery(id+"F0.imprint","IMPRINT",FACE,{"disambiguationData":[TD([[makeQuery(id+"F0.imprint","IMPRINT",EDGE,{"derivedFrom":sQuery(id+"F0.wireOp",EDGE,"E29.2.0.0")}),-1.0]])]});
            var Q5;
            Q5=makeQuery(id+"F0.imprint","IMPRINT",FACE,{"disambiguationData":[TD([[makeQuery(id+"F0.imprint","IMPRINT",EDGE,{"derivedFrom":sQuery(id+"F0.wireOp",EDGE,"E29.2.0.4")}),1.0]])]});
            var Q6;
            Q6=makeQuery(id+"F0.imprint","IMPRINT",FACE,{"disambiguationData":[TD([[makeQuery(id+"F0.imprint","IMPRINT",EDGE,{"derivedFrom":sQuery(id+"F0.wireOp",EDGE,"E29.3.0.0")}),-1.0]])]});
            var Q7;
            Q7=makeQuery(id+"F0.imprint","IMPRINT",FACE,{"disambiguationData":[TD([[makeQuery(id+"F0.imprint","IMPRINT",EDGE,{"derivedFrom":sQuery(id+"F0.wireOp",EDGE,"E29.3.0.4")}),1.0]])]});
            var Q8;
            Q8=makeQuery(id+"F0.imprint","IMPRINT",FACE,{"disambiguationData":[TD([[makeQuery(id+"F0.imprint","IMPRINT",EDGE,{"derivedFrom":sQuery(id+"F0.wireOp",EDGE,"E29.4.0.0")}),-1.0]])]});
            var Q9;
            Q9=makeQuery(id+"F0.imprint","IMPRINT",FACE,{"disambiguationData":[TD([[makeQuery(id+"F0.imprint","IMPRINT",EDGE,{"derivedFrom":sQuery(id+"F0.wireOp",EDGE,"E29.4.0.4")}),1.0]])]});
            var Q10;
            Q10=makeQuery(id+"F0.imprint","IMPRINT",FACE,{"disambiguationData":[TD([[makeQuery(id+"F0.imprint","IMPRINT",EDGE,{"derivedFrom":sQuery(id+"F0.wireOp",EDGE,"E29.5.0.0")}),-1.0]])]});
            var Q11;
            Q11=makeQuery(id+"F0.imprint","IMPRINT",FACE,{"disambiguationData":[TD([[makeQuery(id+"F0.imprint","IMPRINT",EDGE,{"derivedFrom":sQuery(id+"F0.wireOp",EDGE,"E29.5.0.4")}),1.0]])]});
            extrude(context, id + "F1", {"entities" : qUnion([Q0, Q1, Q2, Q3, Q4, Q5, Q6, Q7, Q8, Q9, Q10, Q11]), "depth" : 8 * mm});
        }
        {
            var Q0;
            {var subQ13=sQuery(id+"F0.wireOp",EDGE,"E1");Q0=makeQuery(id+"F0.imprint","IMPRINT",FACE,{"disambiguationData":[TD([[makeQuery(id+"F0.imprint","IMPRINT",EDGE,{"derivedFrom":subQ13}),1.0]])]});}
            extrude(context, id + "F2", {"entities" : qUnion([Q0]), "oppositeDirection" : true, "depth" : 1 * mm});
        }
        {
            var Q0;
            Q0=makeQuery(id+"F0.imprint","IMPRINT",FACE,{"disambiguationData":[TD([[makeQuery(id+"F0.imprint","IMPRINT",EDGE,{"derivedFrom":sQuery(id+"F0.wireOp",EDGE,"E21.bottom")}),-1.0]])]});
            var Q1;
            Q1=makeQuery(id+"F0.imprint","IMPRINT",FACE,{"disambiguationData":[TD([[makeQuery(id+"F0.imprint","IMPRINT",EDGE,{"derivedFrom":sQuery(id+"F0.wireOp",EDGE,"E11.bottom")}),-1.0]])]});
            var Q2;
            Q2=makeQuery(id+"F0.imprint","IMPRINT",FACE,{"disambiguationData":[TD([[makeQuery(id+"F0.imprint","IMPRINT",EDGE,{"derivedFrom":sQuery(id+"F0.wireOp",EDGE,"E17.bottom")}),-1.0]])]});
            var Q3;
            Q3=makeQuery(id+"F0.imprint","IMPRINT",FACE,{"disambiguationData":[TD([[makeQuery(id+"F0.imprint","IMPRINT",EDGE,{"derivedFrom":sQuery(id+"F0.wireOp",EDGE,"E16.bottom")}),-1.0]])]});
            var Q4;
            {var subQ0=sQuery(id+"F0.wireOp",EDGE,"E24.right");Q4=makeQuery(id+"F0.imprint","IMPRINT",FACE,{"disambiguationData":[TD([[makeQuery(id+"F0.imprint","IMPRINT",EDGE,{"derivedFrom":subQ0}),-1.0]])]});}
            var Q5;
            {var subQ0=sQuery(id+"F0.wireOp",EDGE,"E24.left");Q5=makeQuery(id+"F0.imprint","IMPRINT",FACE,{"disambiguationData":[TD([[makeQuery(id+"F0.imprint","IMPRINT",EDGE,{"derivedFrom":subQ0}),1.0]])]});}
            var Q6;
            Q6=makeQuery(id+"F0.imprint","IMPRINT",FACE,{"disambiguationData":[TD([[makeQuery(id+"F0.imprint","IMPRINT",EDGE,{"derivedFrom":sQuery(id+"F0.wireOp",EDGE,"E12.bottom")}),-1.0]])]});
            var Q7;
            Q7=makeQuery(id+"F0.imprint","IMPRINT",FACE,{"disambiguationData":[TD([[makeQuery(id+"F0.imprint","IMPRINT",EDGE,{"derivedFrom":sQuery(id+"F0.wireOp",EDGE,"E30.bottom")}),-1.0]])]});
            var Q8;
            Q8=makeQuery(id+"F0.imprint","IMPRINT",FACE,{"disambiguationData":[TD([[makeQuery(id+"F0.imprint","IMPRINT",EDGE,{"derivedFrom":sQuery(id+"F0.wireOp",EDGE,"E13.bottom")}),-1.0]])]});
            var Q9;
            Q9=makeQuery(id+"F0.imprint","IMPRINT",FACE,{"disambiguationData":[TD([[makeQuery(id+"F0.imprint","IMPRINT",EDGE,{"derivedFrom":sQuery(id+"F0.wireOp",EDGE,"E9.bottom")}),-1.0]])]});
            var Q10;
            Q10=makeQuery(id+"F0.imprint","IMPRINT",FACE,{"disambiguationData":[TD([[makeQuery(id+"F0.imprint","IMPRINT",EDGE,{"derivedFrom":sQuery(id+"F0.wireOp",EDGE,"E10.1.0.0")}),-1.0]])]});
            var Q11;
            Q11=makeQuery(id+"F0.imprint","IMPRINT",FACE,{"disambiguationData":[TD([[makeQuery(id+"F0.imprint","IMPRINT",EDGE,{"derivedFrom":sQuery(id+"F0.wireOp",EDGE,"E10.2.0.0")}),-1.0]])]});
            var Q12;
            Q12=makeQuery(id+"F0.imprint","IMPRINT",FACE,{"disambiguationData":[TD([[makeQuery(id+"F0.imprint","IMPRINT",EDGE,{"derivedFrom":sQuery(id+"F0.wireOp",EDGE,"Ueh38K08-ZFOj-Etvo-b6Af-kDZaYaBKfnBe.bottom")}),-1.0]])]});
            var Q13;
            Q13=makeQuery(id+"F0.imprint","IMPRINT",FACE,{"disambiguationData":[TD([[makeQuery(id+"F0.imprint","IMPRINT",EDGE,{"derivedFrom":sQuery(id+"F0.wireOp",EDGE,"E18.bottom")}),-1.0]])]});
            var Q14;
            Q14=makeQuery(id+"F0.imprint","IMPRINT",FACE,{"disambiguationData":[TD([[makeQuery(id+"F0.imprint","IMPRINT",EDGE,{"derivedFrom":sQuery(id+"F0.wireOp",EDGE,"E19.bottom")}),-1.0]])]});
            extrude(context, id + "F3", {"entities" : qUnion([Q0, Q1, Q2, Q3, Q4, Q5, Q6, Q7, Q8, Q9, Q10, Q11, Q12, Q13, Q14]), "operationType" : NewBodyOperationType.ADD, "depth" : 2 * mm, "hasSecondDirection" : true, "secondDirectionOppositeDirection" : true, "secondDirectionDepth" : 1 * mm});
        }
        {
            var Q0;
            Q0=makeQuery(id+"F0.imprint","IMPRINT",FACE,{"disambiguationData":[TD([[makeQuery(id+"F0.imprint","IMPRINT",EDGE,{"derivedFrom":sQuery(id+"F0.wireOp",EDGE,"E3.bottom")}),-1.0]])]});
            var Q1;
            Q1=makeQuery(id+"F0.imprint","IMPRINT",FACE,{"disambiguationData":[TD([[makeQuery(id+"F0.imprint","IMPRINT",EDGE,{"derivedFrom":sQuery(id+"F0.wireOp",EDGE,"E4.1.0.0")}),-1.0]])]});
            var Q2;
            Q2=makeQuery(id+"F0.imprint","IMPRINT",FACE,{"disambiguationData":[TD([[makeQuery(id+"F0.imprint","IMPRINT",EDGE,{"derivedFrom":sQuery(id+"F0.wireOp",EDGE,"E4.2.0.0")}),-1.0]])]});
            var Q3;
            Q3=makeQuery(id+"F0.imprint","IMPRINT",FACE,{"disambiguationData":[TD([[makeQuery(id+"F0.imprint","IMPRINT",EDGE,{"derivedFrom":sQuery(id+"F0.wireOp",EDGE,"E4.3.0.0")}),-1.0]])]});
            var Q4;
            Q4=makeQuery(id+"F0.imprint","IMPRINT",FACE,{"disambiguationData":[TD([[makeQuery(id+"F0.imprint","IMPRINT",EDGE,{"derivedFrom":sQuery(id+"F0.wireOp",EDGE,"E4.4.0.0")}),-1.0]])]});
            var Q5;
            {var subQ0=sQuery(id+"F0.wireOp",EDGE,"E8");Q5=makeQuery(id+"F0.imprint","IMPRINT",FACE,{"disambiguationData":[TD([[makeQuery(id+"F0.imprint","IMPRINT",EDGE,{"derivedFrom":subQ0}),-1.0]])]});}
            var Q6;
            {var subQ0=sQuery(id+"F0.wireOp",EDGE,"E39");Q6=makeQuery(id+"F0.imprint","IMPRINT",FACE,{"disambiguationData":[TD([[makeQuery(id+"F0.imprint","IMPRINT",EDGE,{"derivedFrom":subQ0}),1.0]])]});}
            var Q7;
            {var subQ0=sQuery(id+"F0.wireOp",EDGE,"E6");Q7=makeQuery(id+"F0.imprint","IMPRINT",FACE,{"disambiguationData":[TD([[makeQuery(id+"F0.imprint","IMPRINT",EDGE,{"derivedFrom":subQ0}),-1.0]])]});}
            extrude(context, id + "F4", {"entities" : qUnion([Q0, Q1, Q2, Q3, Q4, Q5, Q6, Q7]), "operationType" : NewBodyOperationType.ADD, "depth" : 8 * mm, "hasSecondDirection" : true, "secondDirectionOppositeDirection" : true, "secondDirectionDepth" : 1 * mm});
        }
        {
            var Q0;
            Q0=makeQuery(id+"F0.imprint","IMPRINT",FACE,{"disambiguationData":[TD([[makeQuery(id+"F0.imprint","IMPRINT",EDGE,{"derivedFrom":sQuery(id+"F0.wireOp",EDGE,"E20.bottom")}),-1.0]])]});
            var Q1;
            Q1=makeQuery(id+"F0.imprint","IMPRINT",FACE,{"disambiguationData":[TD([[makeQuery(id+"F0.imprint","IMPRINT",EDGE,{"derivedFrom":sQuery(id+"F0.wireOp",EDGE,"E41.bottom")}),-1.0]])]});
            var Q2;
            Q2=makeQuery(id+"F0.imprint","IMPRINT",FACE,{"disambiguationData":[TD([[makeQuery(id+"F0.imprint","IMPRINT",EDGE,{"derivedFrom":sQuery(id+"F0.wireOp",EDGE,"E14.bottom")}),-1.0]])]});
            var Q3;
            Q3=makeQuery(id+"F0.imprint","IMPRINT",FACE,{"disambiguationData":[TD([[makeQuery(id+"F0.imprint","IMPRINT",EDGE,{"derivedFrom":sQuery(id+"F0.wireOp",EDGE,"E109.bottom")}),-1.0]])]});
            extrude(context, id + "F5", {"entities" : qUnion([Q0, Q1, Q2, Q3]), "operationType" : NewBodyOperationType.ADD, "depth" : 2 * mm, "hasSecondDirection" : true, "secondDirectionOppositeDirection" : true, "secondDirectionDepth" : 1 * mm});
        }
        {
            var Q0;
            Q0=makeQuery(id+"F0.imprint","IMPRINT",FACE,{"disambiguationData":[TD([[makeQuery(id+"F0.imprint","IMPRINT",EDGE,{"derivedFrom":sQuery(id+"F0.wireOp",EDGE,"E25.bottom")}),-1.0]])]});
            var Q1;
            Q1=makeQuery(id+"F0.imprint","IMPRINT",FACE,{"disambiguationData":[TD([[makeQuery(id+"F0.imprint","IMPRINT",EDGE,{"derivedFrom":sQuery(id+"F0.wireOp",EDGE,"E26.1.0.0")}),-1.0]])]});
            var Q2;
            Q2=makeQuery(id+"F0.imprint","IMPRINT",FACE,{"disambiguationData":[TD([[makeQuery(id+"F0.imprint","IMPRINT",EDGE,{"derivedFrom":sQuery(id+"F0.wireOp",EDGE,"E26.2.0.0")}),-1.0]])]});
            var Q3;
            Q3=makeQuery(id+"F0.imprint","IMPRINT",FACE,{"disambiguationData":[TD([[makeQuery(id+"F0.imprint","IMPRINT",EDGE,{"derivedFrom":sQuery(id+"F0.wireOp",EDGE,"E26.3.0.0")}),-1.0]])]});
            var Q4;
            Q4=makeQuery(id+"F0.imprint","IMPRINT",FACE,{"disambiguationData":[TD([[makeQuery(id+"F0.imprint","IMPRINT",EDGE,{"derivedFrom":sQuery(id+"F0.wireOp",EDGE,"E26.4.0.0")}),-1.0]])]});
            var Q5;
            Q5=makeQuery(id+"F0.imprint","IMPRINT",FACE,{"disambiguationData":[TD([[makeQuery(id+"F0.imprint","IMPRINT",EDGE,{"derivedFrom":sQuery(id+"F0.wireOp",EDGE,"E26.5.0.0")}),-1.0]])]});
            extrude(context, id + "F6", {"entities" : qUnion([Q0, Q1, Q2, Q3, Q4, Q5]), "depth" : 8 * mm, "hasSecondDirection" : true, "secondDirectionOppositeDirection" : true, "secondDirectionDepth" : 1 * mm});
        }
        {
            var Q0;
            Q0=makeQuery(id+"F0.imprint","IMPRINT",FACE,{"disambiguationData":[TD([[makeQuery(id+"F0.imprint","IMPRINT",EDGE,{"derivedFrom":sQuery(id+"F0.wireOp",EDGE,"E31.bottom")}),-1.0]])]});
            var Q1;
            Q1=makeQuery(id+"F0.imprint","IMPRINT",FACE,{"disambiguationData":[TD([[makeQuery(id+"F0.imprint","IMPRINT",EDGE,{"derivedFrom":sQuery(id+"F0.wireOp",EDGE,"E32.1.0.0")}),1.0]])]});
            var Q2;
            Q2=makeQuery(id+"F0.imprint","IMPRINT",FACE,{"disambiguationData":[TD([[makeQuery(id+"F0.imprint","IMPRINT",EDGE,{"derivedFrom":sQuery(id+"F0.wireOp",EDGE,"E32.2.0.0")}),1.0]])]});
            var Q3;
            Q3=makeQuery(id+"F0.imprint","IMPRINT",FACE,{"disambiguationData":[TD([[makeQuery(id+"F0.imprint","IMPRINT",EDGE,{"derivedFrom":sQuery(id+"F0.wireOp",EDGE,"E32.3.0.0")}),1.0]])]});
            var Q4;
            Q4=makeQuery(id+"F0.imprint","IMPRINT",FACE,{"disambiguationData":[TD([[makeQuery(id+"F0.imprint","IMPRINT",EDGE,{"derivedFrom":sQuery(id+"F0.wireOp",EDGE,"E32.4.0.0")}),1.0]])]});
            var Q5;
            Q5=makeQuery(id+"F0.imprint","IMPRINT",FACE,{"disambiguationData":[TD([[makeQuery(id+"F0.imprint","IMPRINT",EDGE,{"derivedFrom":sQuery(id+"F0.wireOp",EDGE,"E32.5.0.0")}),1.0]])]});
            extrude(context, id + "F7", {"entities" : qUnion([Q0, Q1, Q2, Q3, Q4, Q5]), "operationType" : NewBodyOperationType.ADD, "depth" : 2 * mm, "hasSecondDirection" : true, "secondDirectionOppositeDirection" : true, "secondDirectionDepth" : 1 * mm});
        }
        {
            var Q0;
            Q0=makeQuery(id+"F4.opExtrude","CAP_FACE",FACE,{"disambiguationData":[OSD([sQuery(id+"F0.wireOp",EDGE,"E3.bottom"),sQuery(id+"F0.wireOp",EDGE,"E3.top"),sQuery(id+"F0.wireOp",EDGE,"E3.left"),sQuery(id+"F0.wireOp",EDGE,"E3.right")])],"isStart":false});
            var sketch = newSketch(context, id + "F8", { "sketchPlane" : qUnion([Q0])});
            skPoint(sketch, "E113.endSnap0", {"position": v(4.45, -34.91) * mm});
            skCircle(sketch, "E114", {"center": v(-23.12, -59.32) * mm, "radius": 2.18 * mm});
            skLineSegment(sketch, "E115", {"start": v(-23.12, -59.32) * mm, "end": v(-16.95, -59.32) * mm, "construction": true});
            skCircle(sketch, "E116", {"center": v(-16.95, -59.32) * mm, "radius": 2 * mm});
            skCircle(sketch, "E117.1.0.0", {"center": v(-2.07, -59.32) * mm, "radius": 2 * mm});
            skCircle(sketch, "E117.1.0.1", {"center": v(-8.23, -59.32) * mm, "radius": 2.18 * mm});
            skCircle(sketch, "E117.2.0.0", {"center": v(12.82, -59.32) * mm, "radius": 2 * mm});
            skCircle(sketch, "E117.2.0.1", {"center": v(6.65, -59.32) * mm, "radius": 2.18 * mm});
            skCircle(sketch, "E117.3.0.0", {"center": v(27.7, -59.32) * mm, "radius": 2 * mm});
            skCircle(sketch, "E117.3.0.1", {"center": v(21.54, -59.32) * mm, "radius": 2.18 * mm});
            skCircle(sketch, "E117.4.0.0", {"center": v(42.59, -59.32) * mm, "radius": 2 * mm});
            skCircle(sketch, "E117.4.0.1", {"center": v(36.43, -59.32) * mm, "radius": 2.18 * mm});
            skLineSegment(sketch, "E117.direction1", {"start": v(-16.95, -59.32) * mm, "end": v(-2.07, -59.32) * mm, "construction": true});
            skLineSegment(sketch, "E118", {"start": v(84.72, -59.76) * mm, "end": v(93.91, -59.76) * mm, "construction": true});
            skCircle(sketch, "E119", {"center": v(84.72, -59.76) * mm, "radius": 2.5 * mm});
            skCircle(sketch, "E120", {"center": v(93.91, -59.76) * mm, "radius": 2.5 * mm});
            skCircle(sketch, "E121.1.0.0", {"center": v(102.63, -59.76) * mm, "radius": 2.5 * mm});
            skCircle(sketch, "E121.1.0.1", {"center": v(111.82, -59.76) * mm, "radius": 2.5 * mm});
            skCircle(sketch, "E121.2.0.0", {"center": v(120.53, -59.76) * mm, "radius": 2.5 * mm});
            skCircle(sketch, "E121.2.0.1", {"center": v(129.73, -59.76) * mm, "radius": 2.5 * mm});
            skLineSegment(sketch, "E121.direction1", {"start": v(84.72, -59.76) * mm, "end": v(102.63, -59.76) * mm, "construction": true});
            skSolve(sketch);
        }
        {
            var Q0;
            Q0=makeQuery(id+"F8.imprint","IMPRINT",FACE,{"disambiguationData":[TD([[makeQuery(id+"F8.imprint","IMPRINT",EDGE,{"derivedFrom":sQuery(id+"F8.wireOp",EDGE,"E114")}),1.0]])]});
            var Q1;
            Q1=makeQuery(id+"F8.imprint","IMPRINT",FACE,{"disambiguationData":[TD([[makeQuery(id+"F8.imprint","IMPRINT",EDGE,{"derivedFrom":sQuery(id+"F8.wireOp",EDGE,"E116")}),1.0]])]});
            var Q2;
            Q2=makeQuery(id+"F8.imprint","IMPRINT",FACE,{"disambiguationData":[TD([[makeQuery(id+"F8.imprint","IMPRINT",EDGE,{"derivedFrom":sQuery(id+"F8.wireOp",EDGE,"E117.1.0.1")}),1.0]])]});
            var Q3;
            Q3=makeQuery(id+"F8.imprint","IMPRINT",FACE,{"disambiguationData":[TD([[makeQuery(id+"F8.imprint","IMPRINT",EDGE,{"derivedFrom":sQuery(id+"F8.wireOp",EDGE,"E117.1.0.0")}),1.0]])]});
            var Q4;
            Q4=makeQuery(id+"F8.imprint","IMPRINT",FACE,{"disambiguationData":[TD([[makeQuery(id+"F8.imprint","IMPRINT",EDGE,{"derivedFrom":sQuery(id+"F8.wireOp",EDGE,"E117.2.0.1")}),1.0]])]});
            var Q5;
            Q5=makeQuery(id+"F8.imprint","IMPRINT",FACE,{"disambiguationData":[TD([[makeQuery(id+"F8.imprint","IMPRINT",EDGE,{"derivedFrom":sQuery(id+"F8.wireOp",EDGE,"E117.2.0.0")}),1.0]])]});
            var Q6;
            Q6=makeQuery(id+"F8.imprint","IMPRINT",FACE,{"disambiguationData":[TD([[makeQuery(id+"F8.imprint","IMPRINT",EDGE,{"derivedFrom":sQuery(id+"F8.wireOp",EDGE,"E117.3.0.1")}),1.0]])]});
            var Q7;
            Q7=makeQuery(id+"F8.imprint","IMPRINT",FACE,{"disambiguationData":[TD([[makeQuery(id+"F8.imprint","IMPRINT",EDGE,{"derivedFrom":sQuery(id+"F8.wireOp",EDGE,"E117.3.0.0")}),1.0]])]});
            var Q8;
            Q8=makeQuery(id+"F8.imprint","IMPRINT",FACE,{"disambiguationData":[TD([[makeQuery(id+"F8.imprint","IMPRINT",EDGE,{"derivedFrom":sQuery(id+"F8.wireOp",EDGE,"E117.4.0.1")}),1.0]])]});
            var Q9;
            Q9=makeQuery(id+"F8.imprint","IMPRINT",FACE,{"disambiguationData":[TD([[makeQuery(id+"F8.imprint","IMPRINT",EDGE,{"derivedFrom":sQuery(id+"F8.wireOp",EDGE,"E117.4.0.0")}),1.0]])]});
            var Q10;
            Q10=makeQuery(id+"F8.imprint","IMPRINT",FACE,{"disambiguationData":[TD([[makeQuery(id+"F8.imprint","IMPRINT",EDGE,{"derivedFrom":sQuery(id+"F8.wireOp",EDGE,"E119")}),1.0]])]});
            var Q11;
            Q11=makeQuery(id+"F8.imprint","IMPRINT",FACE,{"disambiguationData":[TD([[makeQuery(id+"F8.imprint","IMPRINT",EDGE,{"derivedFrom":sQuery(id+"F8.wireOp",EDGE,"E120")}),1.0]])]});
            var Q12;
            Q12=makeQuery(id+"F8.imprint","IMPRINT",FACE,{"disambiguationData":[TD([[makeQuery(id+"F8.imprint","IMPRINT",EDGE,{"derivedFrom":sQuery(id+"F8.wireOp",EDGE,"E121.1.0.0")}),1.0]])]});
            var Q13;
            Q13=makeQuery(id+"F8.imprint","IMPRINT",FACE,{"disambiguationData":[TD([[makeQuery(id+"F8.imprint","IMPRINT",EDGE,{"derivedFrom":sQuery(id+"F8.wireOp",EDGE,"E121.1.0.1")}),1.0]])]});
            var Q14;
            Q14=makeQuery(id+"F8.imprint","IMPRINT",FACE,{"disambiguationData":[TD([[makeQuery(id+"F8.imprint","IMPRINT",EDGE,{"derivedFrom":sQuery(id+"F8.wireOp",EDGE,"E121.2.0.0")}),1.0]])]});
            var Q15;
            Q15=makeQuery(id+"F8.imprint","IMPRINT",FACE,{"disambiguationData":[TD([[makeQuery(id+"F8.imprint","IMPRINT",EDGE,{"derivedFrom":sQuery(id+"F8.wireOp",EDGE,"E121.2.0.1")}),1.0]])]});
            extrude(context, id + "F9", {"entities" : qUnion([Q0, Q1, Q2, Q3, Q4, Q5, Q6, Q7, Q8, Q9, Q10, Q11, Q12, Q13, Q14, Q15]), "operationType" : NewBodyOperationType.REMOVE, "oppositeDirection" : true, "depth" : 4 * mm});
        }
        {
            var Q0;
            Q0=makeQuery(id+"F0.imprint","IMPRINT",FACE,{"disambiguationData":[TD([[makeQuery(id+"F0.imprint","IMPRINT",EDGE,{"derivedFrom":sQuery(id+"F0.wireOp",EDGE,"E49.2.0.5")}),1.0]])]});
            var Q1;
            Q1=makeQuery(id+"F0.imprint","IMPRINT",FACE,{"disambiguationData":[TD([[makeQuery(id+"F0.imprint","IMPRINT",EDGE,{"derivedFrom":sQuery(id+"F0.wireOp",EDGE,"E49.1.0.5")}),1.0]])]});
            var Q2;
            Q2=makeQuery(id+"F0.imprint","IMPRINT",FACE,{"disambiguationData":[TD([[makeQuery(id+"F0.imprint","IMPRINT",EDGE,{"derivedFrom":sQuery(id+"F0.wireOp",EDGE,"E48.5.0.0")}),1.0]])]});
            var Q3;
            Q3=makeQuery(id+"F0.imprint","IMPRINT",FACE,{"disambiguationData":[TD([[makeQuery(id+"F0.imprint","IMPRINT",EDGE,{"derivedFrom":sQuery(id+"F0.wireOp",EDGE,"E48.4.0.0")}),1.0]])]});
            var Q4;
            Q4=makeQuery(id+"F0.imprint","IMPRINT",FACE,{"disambiguationData":[TD([[makeQuery(id+"F0.imprint","IMPRINT",EDGE,{"derivedFrom":sQuery(id+"F0.wireOp",EDGE,"E49.1.0.4")}),1.0]])]});
            var Q5;
            Q5=makeQuery(id+"F0.imprint","IMPRINT",FACE,{"disambiguationData":[TD([[makeQuery(id+"F0.imprint","IMPRINT",EDGE,{"derivedFrom":sQuery(id+"F0.wireOp",EDGE,"E49.2.0.4")}),1.0]])]});
            var Q6;
            Q6=makeQuery(id+"F0.imprint","IMPRINT",FACE,{"disambiguationData":[TD([[makeQuery(id+"F0.imprint","IMPRINT",EDGE,{"derivedFrom":sQuery(id+"F0.wireOp",EDGE,"E49.2.0.3")}),1.0]])]});
            var Q7;
            Q7=makeQuery(id+"F0.imprint","IMPRINT",FACE,{"disambiguationData":[TD([[makeQuery(id+"F0.imprint","IMPRINT",EDGE,{"derivedFrom":sQuery(id+"F0.wireOp",EDGE,"E49.1.0.3")}),1.0]])]});
            var Q8;
            Q8=makeQuery(id+"F0.imprint","IMPRINT",FACE,{"disambiguationData":[TD([[makeQuery(id+"F0.imprint","IMPRINT",EDGE,{"derivedFrom":sQuery(id+"F0.wireOp",EDGE,"E48.3.0.0")}),1.0]])]});
            var Q9;
            Q9=makeQuery(id+"F0.imprint","IMPRINT",FACE,{"disambiguationData":[TD([[makeQuery(id+"F0.imprint","IMPRINT",EDGE,{"derivedFrom":sQuery(id+"F0.wireOp",EDGE,"E49.2.0.2")}),1.0]])]});
            var Q10;
            Q10=makeQuery(id+"F0.imprint","IMPRINT",FACE,{"disambiguationData":[TD([[makeQuery(id+"F0.imprint","IMPRINT",EDGE,{"derivedFrom":sQuery(id+"F0.wireOp",EDGE,"E49.2.0.1")}),1.0]])]});
            var Q11;
            Q11=makeQuery(id+"F0.imprint","IMPRINT",FACE,{"disambiguationData":[TD([[makeQuery(id+"F0.imprint","IMPRINT",EDGE,{"derivedFrom":sQuery(id+"F0.wireOp",EDGE,"E49.1.0.1")}),1.0]])]});
            var Q12;
            Q12=makeQuery(id+"F0.imprint","IMPRINT",FACE,{"disambiguationData":[TD([[makeQuery(id+"F0.imprint","IMPRINT",EDGE,{"derivedFrom":sQuery(id+"F0.wireOp",EDGE,"E49.1.0.2")}),1.0]])]});
            var Q13;
            Q13=makeQuery(id+"F0.imprint","IMPRINT",FACE,{"disambiguationData":[TD([[makeQuery(id+"F0.imprint","IMPRINT",EDGE,{"derivedFrom":sQuery(id+"F0.wireOp",EDGE,"E48.2.0.0")}),1.0]])]});
            var Q14;
            Q14=makeQuery(id+"F0.imprint","IMPRINT",FACE,{"disambiguationData":[TD([[makeQuery(id+"F0.imprint","IMPRINT",EDGE,{"derivedFrom":sQuery(id+"F0.wireOp",EDGE,"E48.1.0.0")}),1.0]])]});
            var Q15;
            Q15=makeQuery(id+"F0.imprint","IMPRINT",FACE,{"disambiguationData":[TD([[makeQuery(id+"F0.imprint","IMPRINT",EDGE,{"derivedFrom":sQuery(id+"F0.wireOp",EDGE,"E47")}),1.0]])]});
            var Q16;
            Q16=makeQuery(id+"F0.imprint","IMPRINT",FACE,{"disambiguationData":[TD([[makeQuery(id+"F0.imprint","IMPRINT",EDGE,{"derivedFrom":sQuery(id+"F0.wireOp",EDGE,"E49.1.0.0")}),1.0]])]});
            var Q17;
            Q17=makeQuery(id+"F0.imprint","IMPRINT",FACE,{"disambiguationData":[TD([[makeQuery(id+"F0.imprint","IMPRINT",EDGE,{"derivedFrom":sQuery(id+"F0.wireOp",EDGE,"E49.2.0.0")}),1.0]])]});
            var Q18;
            Q18=makeQuery(id+"F0.imprint","IMPRINT",FACE,{"disambiguationData":[TD([[makeQuery(id+"F0.imprint","IMPRINT",EDGE,{"derivedFrom":sQuery(id+"F0.wireOp",EDGE,"E55.6.0.0")}),1.0]])]});
            var Q19;
            Q19=makeQuery(id+"F0.imprint","IMPRINT",FACE,{"disambiguationData":[TD([[makeQuery(id+"F0.imprint","IMPRINT",EDGE,{"derivedFrom":sQuery(id+"F0.wireOp",EDGE,"E51")}),1.0]])]});
            var Q20;
            Q20=makeQuery(id+"F0.imprint","IMPRINT",FACE,{"disambiguationData":[TD([[makeQuery(id+"F0.imprint","IMPRINT",EDGE,{"derivedFrom":sQuery(id+"F0.wireOp",EDGE,"E52.MirrorC")}),-1.0]])]});
            var Q21;
            Q21=makeQuery(id+"F0.imprint","IMPRINT",FACE,{"disambiguationData":[TD([[makeQuery(id+"F0.imprint","IMPRINT",EDGE,{"derivedFrom":sQuery(id+"F0.wireOp",EDGE,"E61.MirrorC")}),-1.0]])]});
            var Q22;
            Q22=makeQuery(id+"F0.imprint","IMPRINT",FACE,{"disambiguationData":[TD([[makeQuery(id+"F0.imprint","IMPRINT",EDGE,{"derivedFrom":sQuery(id+"F0.wireOp",EDGE,"E69")}),1.0]])]});
            var Q23;
            Q23=makeQuery(id+"F0.imprint","IMPRINT",FACE,{"disambiguationData":[TD([[makeQuery(id+"F0.imprint","IMPRINT",EDGE,{"derivedFrom":sQuery(id+"F0.wireOp",EDGE,"E70.MirrorC")}),-1.0]])]});
            var Q24;
            Q24=makeQuery(id+"F0.imprint","IMPRINT",FACE,{"disambiguationData":[TD([[makeQuery(id+"F0.imprint","IMPRINT",EDGE,{"derivedFrom":sQuery(id+"F0.wireOp",EDGE,"E64.2.0.0")}),1.0]])]});
            var Q25;
            Q25=makeQuery(id+"F0.imprint","IMPRINT",FACE,{"disambiguationData":[TD([[makeQuery(id+"F0.imprint","IMPRINT",EDGE,{"derivedFrom":sQuery(id+"F0.wireOp",EDGE,"E65.MirrorC")}),-1.0]])]});
            var Q26;
            Q26=makeQuery(id+"F0.imprint","IMPRINT",FACE,{"disambiguationData":[TD([[makeQuery(id+"F0.imprint","IMPRINT",EDGE,{"derivedFrom":sQuery(id+"F0.wireOp",EDGE,"E64.1.0.0")}),1.0]])]});
            var Q27;
            Q27=makeQuery(id+"F0.imprint","IMPRINT",FACE,{"disambiguationData":[TD([[makeQuery(id+"F0.imprint","IMPRINT",EDGE,{"derivedFrom":sQuery(id+"F0.wireOp",EDGE,"E66.MirrorC")}),-1.0]])]});
            var Q28;
            Q28=makeQuery(id+"F0.imprint","IMPRINT",FACE,{"disambiguationData":[TD([[makeQuery(id+"F0.imprint","IMPRINT",EDGE,{"derivedFrom":sQuery(id+"F0.wireOp",EDGE,"E63")}),1.0]])]});
            var Q29;
            Q29=makeQuery(id+"F0.imprint","IMPRINT",FACE,{"disambiguationData":[TD([[makeQuery(id+"F0.imprint","IMPRINT",EDGE,{"derivedFrom":sQuery(id+"F0.wireOp",EDGE,"E68.MirrorC")}),-1.0]])]});
            var Q30;
            Q30=makeQuery(id+"F0.imprint","IMPRINT",FACE,{"disambiguationData":[TD([[makeQuery(id+"F0.imprint","IMPRINT",EDGE,{"derivedFrom":sQuery(id+"F0.wireOp",EDGE,"E55.5.0.0")}),1.0]])]});
            var Q31;
            Q31=makeQuery(id+"F0.imprint","IMPRINT",FACE,{"disambiguationData":[TD([[makeQuery(id+"F0.imprint","IMPRINT",EDGE,{"derivedFrom":sQuery(id+"F0.wireOp",EDGE,"E59.MirrorC")}),-1.0]])]});
            var Q32;
            Q32=makeQuery(id+"F0.imprint","IMPRINT",FACE,{"disambiguationData":[TD([[makeQuery(id+"F0.imprint","IMPRINT",EDGE,{"derivedFrom":sQuery(id+"F0.wireOp",EDGE,"E58.MirrorC")}),-1.0]])]});
            var Q33;
            Q33=makeQuery(id+"F0.imprint","IMPRINT",FACE,{"disambiguationData":[TD([[makeQuery(id+"F0.imprint","IMPRINT",EDGE,{"derivedFrom":sQuery(id+"F0.wireOp",EDGE,"E55.4.0.0")}),1.0]])]});
            var Q34;
            Q34=makeQuery(id+"F0.imprint","IMPRINT",FACE,{"disambiguationData":[TD([[makeQuery(id+"F0.imprint","IMPRINT",EDGE,{"derivedFrom":sQuery(id+"F0.wireOp",EDGE,"E55.3.0.0")}),1.0]])]});
            var Q35;
            Q35=makeQuery(id+"F0.imprint","IMPRINT",FACE,{"disambiguationData":[TD([[makeQuery(id+"F0.imprint","IMPRINT",EDGE,{"derivedFrom":sQuery(id+"F0.wireOp",EDGE,"E60.MirrorC")}),-1.0]])]});
            var Q36;
            Q36=makeQuery(id+"F0.imprint","IMPRINT",FACE,{"disambiguationData":[TD([[makeQuery(id+"F0.imprint","IMPRINT",EDGE,{"derivedFrom":sQuery(id+"F0.wireOp",EDGE,"E55.2.0.0")}),1.0]])]});
            var Q37;
            Q37=makeQuery(id+"F0.imprint","IMPRINT",FACE,{"disambiguationData":[TD([[makeQuery(id+"F0.imprint","IMPRINT",EDGE,{"derivedFrom":sQuery(id+"F0.wireOp",EDGE,"E57.MirrorC")}),-1.0]])]});
            var Q38;
            Q38=makeQuery(id+"F0.imprint","IMPRINT",FACE,{"disambiguationData":[TD([[makeQuery(id+"F0.imprint","IMPRINT",EDGE,{"derivedFrom":sQuery(id+"F0.wireOp",EDGE,"E55.1.0.0")}),1.0]])]});
            var Q39;
            Q39=makeQuery(id+"F0.imprint","IMPRINT",FACE,{"disambiguationData":[TD([[makeQuery(id+"F0.imprint","IMPRINT",EDGE,{"derivedFrom":sQuery(id+"F0.wireOp",EDGE,"E56.MirrorC")}),-1.0]])]});
            var Q40;
            Q40=makeQuery(id+"F0.imprint","IMPRINT",FACE,{"disambiguationData":[TD([[makeQuery(id+"F0.imprint","IMPRINT",EDGE,{"derivedFrom":sQuery(id+"F0.wireOp",EDGE,"E53")}),1.0]])]});
            var Q41;
            Q41=makeQuery(id+"F0.imprint","IMPRINT",FACE,{"disambiguationData":[TD([[makeQuery(id+"F0.imprint","IMPRINT",EDGE,{"derivedFrom":sQuery(id+"F0.wireOp",EDGE,"E54.MirrorC")}),-1.0]])]});
            var Q42;
            Q42=makeQuery(id+"F0.imprint","IMPRINT",FACE,{"disambiguationData":[TD([[makeQuery(id+"F0.imprint","IMPRINT",EDGE,{"derivedFrom":sQuery(id+"F0.wireOp",EDGE,"E72.9.0.0")}),1.0]])]});
            var Q43;
            Q43=makeQuery(id+"F0.imprint","IMPRINT",FACE,{"disambiguationData":[TD([[makeQuery(id+"F0.imprint","IMPRINT",EDGE,{"derivedFrom":sQuery(id+"F0.wireOp",EDGE,"E72.8.0.0")}),1.0]])]});
            var Q44;
            Q44=makeQuery(id+"F0.imprint","IMPRINT",FACE,{"disambiguationData":[TD([[makeQuery(id+"F0.imprint","IMPRINT",EDGE,{"derivedFrom":sQuery(id+"F0.wireOp",EDGE,"E72.7.0.0")}),1.0]])]});
            var Q45;
            Q45=makeQuery(id+"F0.imprint","IMPRINT",FACE,{"disambiguationData":[TD([[makeQuery(id+"F0.imprint","IMPRINT",EDGE,{"derivedFrom":sQuery(id+"F0.wireOp",EDGE,"E72.6.0.0")}),1.0]])]});
            var Q46;
            Q46=makeQuery(id+"F0.imprint","IMPRINT",FACE,{"disambiguationData":[TD([[makeQuery(id+"F0.imprint","IMPRINT",EDGE,{"derivedFrom":sQuery(id+"F0.wireOp",EDGE,"E72.5.0.0")}),1.0]])]});
            var Q47;
            Q47=makeQuery(id+"F0.imprint","IMPRINT",FACE,{"disambiguationData":[TD([[makeQuery(id+"F0.imprint","IMPRINT",EDGE,{"derivedFrom":sQuery(id+"F0.wireOp",EDGE,"E72.4.0.0")}),1.0]])]});
            var Q48;
            Q48=makeQuery(id+"F0.imprint","IMPRINT",FACE,{"disambiguationData":[TD([[makeQuery(id+"F0.imprint","IMPRINT",EDGE,{"derivedFrom":sQuery(id+"F0.wireOp",EDGE,"E72.3.0.0")}),1.0]])]});
            var Q49;
            Q49=makeQuery(id+"F0.imprint","IMPRINT",FACE,{"disambiguationData":[TD([[makeQuery(id+"F0.imprint","IMPRINT",EDGE,{"derivedFrom":sQuery(id+"F0.wireOp",EDGE,"E72.2.0.0")}),1.0]])]});
            var Q50;
            Q50=makeQuery(id+"F0.imprint","IMPRINT",FACE,{"disambiguationData":[TD([[makeQuery(id+"F0.imprint","IMPRINT",EDGE,{"derivedFrom":sQuery(id+"F0.wireOp",EDGE,"E71")}),1.0]])]});
            var Q51;
            Q51=makeQuery(id+"F0.imprint","IMPRINT",FACE,{"disambiguationData":[TD([[makeQuery(id+"F0.imprint","IMPRINT",EDGE,{"derivedFrom":sQuery(id+"F0.wireOp",EDGE,"E72.1.0.0")}),1.0]])]});
            var Q52;
            Q52=makeQuery(id+"F0.imprint","IMPRINT",FACE,{"disambiguationData":[TD([[makeQuery(id+"F0.imprint","IMPRINT",EDGE,{"derivedFrom":sQuery(id+"F0.wireOp",EDGE,"E73")}),1.0]])]});
            var Q53;
            Q53=makeQuery(id+"F0.imprint","IMPRINT",FACE,{"disambiguationData":[TD([[makeQuery(id+"F0.imprint","IMPRINT",EDGE,{"derivedFrom":sQuery(id+"F0.wireOp",EDGE,"E75.1.0.0")}),1.0]])]});
            var Q54;
            Q54=makeQuery(id+"F0.imprint","IMPRINT",FACE,{"disambiguationData":[TD([[makeQuery(id+"F0.imprint","IMPRINT",EDGE,{"derivedFrom":sQuery(id+"F0.wireOp",EDGE,"E75.2.0.0")}),1.0]])]});
            var Q55;
            Q55=makeQuery(id+"F0.imprint","IMPRINT",FACE,{"disambiguationData":[TD([[makeQuery(id+"F0.imprint","IMPRINT",EDGE,{"derivedFrom":sQuery(id+"F0.wireOp",EDGE,"E74.1.0.0")}),1.0]])]});
            var Q56;
            Q56=makeQuery(id+"F0.imprint","IMPRINT",FACE,{"disambiguationData":[TD([[makeQuery(id+"F0.imprint","IMPRINT",EDGE,{"derivedFrom":sQuery(id+"F0.wireOp",EDGE,"E75.1.0.1")}),1.0]])]});
            var Q57;
            Q57=makeQuery(id+"F0.imprint","IMPRINT",FACE,{"disambiguationData":[TD([[makeQuery(id+"F0.imprint","IMPRINT",EDGE,{"derivedFrom":sQuery(id+"F0.wireOp",EDGE,"E75.2.0.1")}),1.0]])]});
            var Q58;
            Q58=makeQuery(id+"F0.imprint","IMPRINT",FACE,{"disambiguationData":[TD([[makeQuery(id+"F0.imprint","IMPRINT",EDGE,{"derivedFrom":sQuery(id+"F0.wireOp",EDGE,"E74.2.0.0")}),1.0]])]});
            var Q59;
            Q59=makeQuery(id+"F0.imprint","IMPRINT",FACE,{"disambiguationData":[TD([[makeQuery(id+"F0.imprint","IMPRINT",EDGE,{"derivedFrom":sQuery(id+"F0.wireOp",EDGE,"E75.1.0.2")}),1.0]])]});
            var Q60;
            Q60=makeQuery(id+"F0.imprint","IMPRINT",FACE,{"disambiguationData":[TD([[makeQuery(id+"F0.imprint","IMPRINT",EDGE,{"derivedFrom":sQuery(id+"F0.wireOp",EDGE,"E75.2.0.2")}),1.0]])]});
            var Q61;
            Q61=makeQuery(id+"F0.imprint","IMPRINT",FACE,{"disambiguationData":[TD([[makeQuery(id+"F0.imprint","IMPRINT",EDGE,{"derivedFrom":sQuery(id+"F0.wireOp",EDGE,"E94.4.0.0")}),1.0]])]});
            var Q62;
            Q62=makeQuery(id+"F0.imprint","IMPRINT",FACE,{"disambiguationData":[TD([[makeQuery(id+"F0.imprint","IMPRINT",EDGE,{"derivedFrom":sQuery(id+"F0.wireOp",EDGE,"E95.MirrorC")}),-1.0]])]});
            var Q63;
            Q63=makeQuery(id+"F0.imprint","IMPRINT",FACE,{"disambiguationData":[TD([[makeQuery(id+"F0.imprint","IMPRINT",EDGE,{"derivedFrom":sQuery(id+"F0.wireOp",EDGE,"E94.3.0.0")}),1.0]])]});
            var Q64;
            Q64=makeQuery(id+"F0.imprint","IMPRINT",FACE,{"disambiguationData":[TD([[makeQuery(id+"F0.imprint","IMPRINT",EDGE,{"derivedFrom":sQuery(id+"F0.wireOp",EDGE,"E96.MirrorC")}),-1.0]])]});
            var Q65;
            Q65=makeQuery(id+"F0.imprint","IMPRINT",FACE,{"disambiguationData":[TD([[makeQuery(id+"F0.imprint","IMPRINT",EDGE,{"derivedFrom":sQuery(id+"F0.wireOp",EDGE,"E94.2.0.0")}),1.0]])]});
            var Q66;
            Q66=makeQuery(id+"F0.imprint","IMPRINT",FACE,{"disambiguationData":[TD([[makeQuery(id+"F0.imprint","IMPRINT",EDGE,{"derivedFrom":sQuery(id+"F0.wireOp",EDGE,"E97.MirrorC")}),-1.0]])]});
            var Q67;
            Q67=makeQuery(id+"F0.imprint","IMPRINT",FACE,{"disambiguationData":[TD([[makeQuery(id+"F0.imprint","IMPRINT",EDGE,{"derivedFrom":sQuery(id+"F0.wireOp",EDGE,"E94.1.0.0")}),1.0]])]});
            var Q68;
            Q68=makeQuery(id+"F0.imprint","IMPRINT",FACE,{"disambiguationData":[TD([[makeQuery(id+"F0.imprint","IMPRINT",EDGE,{"derivedFrom":sQuery(id+"F0.wireOp",EDGE,"E98.MirrorC")}),-1.0]])]});
            var Q69;
            Q69=makeQuery(id+"F0.imprint","IMPRINT",FACE,{"disambiguationData":[TD([[makeQuery(id+"F0.imprint","IMPRINT",EDGE,{"derivedFrom":sQuery(id+"F0.wireOp",EDGE,"E93")}),1.0]])]});
            var Q70;
            Q70=makeQuery(id+"F0.imprint","IMPRINT",FACE,{"disambiguationData":[TD([[makeQuery(id+"F0.imprint","IMPRINT",EDGE,{"derivedFrom":sQuery(id+"F0.wireOp",EDGE,"E99.MirrorC")}),-1.0]])]});
            var Q71;
            Q71=makeQuery(id+"F0.imprint","IMPRINT",FACE,{"disambiguationData":[TD([[makeQuery(id+"F0.imprint","IMPRINT",EDGE,{"derivedFrom":sQuery(id+"F0.wireOp",EDGE,"E90")}),1.0]])]});
            var Q72;
            Q72=makeQuery(id+"F0.imprint","IMPRINT",FACE,{"disambiguationData":[TD([[makeQuery(id+"F0.imprint","IMPRINT",EDGE,{"derivedFrom":sQuery(id+"F0.wireOp",EDGE,"E91.1.0.0")}),1.0]])]});
            var Q73;
            Q73=makeQuery(id+"F0.imprint","IMPRINT",FACE,{"disambiguationData":[TD([[makeQuery(id+"F0.imprint","IMPRINT",EDGE,{"derivedFrom":sQuery(id+"F0.wireOp",EDGE,"E91.2.0.0")}),1.0]])]});
            var Q74;
            Q74=makeQuery(id+"F0.imprint","IMPRINT",FACE,{"disambiguationData":[TD([[makeQuery(id+"F0.imprint","IMPRINT",EDGE,{"derivedFrom":sQuery(id+"F0.wireOp",EDGE,"9d7452ca-5238-4874-b6d6-7091a39b5f7d0.MirrorC")}),-1.0]])]});
            var Q75;
            Q75=makeQuery(id+"F0.imprint","IMPRINT",FACE,{"disambiguationData":[TD([[makeQuery(id+"F0.imprint","IMPRINT",EDGE,{"derivedFrom":sQuery(id+"F0.wireOp",EDGE,"cd3f2751-9803-46e5-85fe-3ac526f2670b0.MirrorC")}),-1.0]])]});
            var Q76;
            Q76=makeQuery(id+"F0.imprint","IMPRINT",FACE,{"disambiguationData":[TD([[makeQuery(id+"F0.imprint","IMPRINT",EDGE,{"derivedFrom":sQuery(id+"F0.wireOp",EDGE,"f5ae9079-3a14-4a98-92a8-fd5d41ba24410.MirrorC")}),-1.0]])]});
            var Q77;
            Q77=makeQuery(id+"F0.imprint","IMPRINT",FACE,{"disambiguationData":[TD([[makeQuery(id+"F0.imprint","IMPRINT",EDGE,{"derivedFrom":sQuery(id+"F0.wireOp",EDGE,"kWTZdkEn-rmND-m3uX-E6a4-7ZHOFMzGF33a")}),1.0]])]});
            var Q78;
            Q78=makeQuery(id+"F0.imprint","IMPRINT",FACE,{"disambiguationData":[TD([[makeQuery(id+"F0.imprint","IMPRINT",EDGE,{"derivedFrom":sQuery(id+"F0.wireOp",EDGE,"2ed4a6e4-95d2-4081-b7fa-416d100f7593.1.0.0")}),1.0]])]});
            var Q79;
            Q79=makeQuery(id+"F0.imprint","IMPRINT",FACE,{"disambiguationData":[TD([[makeQuery(id+"F0.imprint","IMPRINT",EDGE,{"derivedFrom":sQuery(id+"F0.wireOp",EDGE,"2ed4a6e4-95d2-4081-b7fa-416d100f7593.2.0.0")}),1.0]])]});
            var Q80;
            Q80=makeQuery(id+"F0.imprint","IMPRINT",FACE,{"disambiguationData":[TD([[makeQuery(id+"F0.imprint","IMPRINT",EDGE,{"derivedFrom":sQuery(id+"F0.wireOp",EDGE,"E88.MirrorC")}),-1.0]])]});
            var Q81;
            Q81=makeQuery(id+"F0.imprint","IMPRINT",FACE,{"disambiguationData":[TD([[makeQuery(id+"F0.imprint","IMPRINT",EDGE,{"derivedFrom":sQuery(id+"F0.wireOp",EDGE,"E89.MirrorC")}),1.0]])]});
            var Q82;
            Q82=makeQuery(id+"F0.imprint","IMPRINT",FACE,{"disambiguationData":[TD([[makeQuery(id+"F0.imprint","IMPRINT",EDGE,{"derivedFrom":sQuery(id+"F0.wireOp",EDGE,"E86.MirrorC")}),-1.0]])]});
            var Q83;
            Q83=makeQuery(id+"F0.imprint","IMPRINT",FACE,{"disambiguationData":[TD([[makeQuery(id+"F0.imprint","IMPRINT",EDGE,{"derivedFrom":sQuery(id+"F0.wireOp",EDGE,"E87.MirrorC")}),1.0]])]});
            var Q84;
            Q84=makeQuery(id+"F0.imprint","IMPRINT",FACE,{"disambiguationData":[TD([[makeQuery(id+"F0.imprint","IMPRINT",EDGE,{"derivedFrom":sQuery(id+"F0.wireOp",EDGE,"E84.MirrorC")}),-1.0]])]});
            var Q85;
            Q85=makeQuery(id+"F0.imprint","IMPRINT",FACE,{"disambiguationData":[TD([[makeQuery(id+"F0.imprint","IMPRINT",EDGE,{"derivedFrom":sQuery(id+"F0.wireOp",EDGE,"E85.MirrorC")}),1.0]])]});
            var Q86;
            Q86=makeQuery(id+"F0.imprint","IMPRINT",FACE,{"disambiguationData":[TD([[makeQuery(id+"F0.imprint","IMPRINT",EDGE,{"derivedFrom":sQuery(id+"F0.wireOp",EDGE,"E82.MirrorC")}),-1.0]])]});
            var Q87;
            Q87=makeQuery(id+"F0.imprint","IMPRINT",FACE,{"disambiguationData":[TD([[makeQuery(id+"F0.imprint","IMPRINT",EDGE,{"derivedFrom":sQuery(id+"F0.wireOp",EDGE,"E83.MirrorC")}),1.0]])]});
            var Q88;
            Q88=makeQuery(id+"F0.imprint","IMPRINT",FACE,{"disambiguationData":[TD([[makeQuery(id+"F0.imprint","IMPRINT",EDGE,{"derivedFrom":sQuery(id+"F0.wireOp",EDGE,"E80.MirrorC")}),-1.0]])]});
            var Q89;
            Q89=makeQuery(id+"F0.imprint","IMPRINT",FACE,{"disambiguationData":[TD([[makeQuery(id+"F0.imprint","IMPRINT",EDGE,{"derivedFrom":sQuery(id+"F0.wireOp",EDGE,"E81.MirrorC")}),1.0]])]});
            var Q90;
            Q90=makeQuery(id+"F0.imprint","IMPRINT",FACE,{"disambiguationData":[TD([[makeQuery(id+"F0.imprint","IMPRINT",EDGE,{"derivedFrom":sQuery(id+"F0.wireOp",EDGE,"E79.4.0.0")}),1.0]])]});
            var Q91;
            Q91=makeQuery(id+"F0.imprint","IMPRINT",FACE,{"disambiguationData":[TD([[makeQuery(id+"F0.imprint","IMPRINT",EDGE,{"derivedFrom":sQuery(id+"F0.wireOp",EDGE,"E79.4.0.1")}),-1.0]])]});
            var Q92;
            Q92=makeQuery(id+"F0.imprint","IMPRINT",FACE,{"disambiguationData":[TD([[makeQuery(id+"F0.imprint","IMPRINT",EDGE,{"derivedFrom":sQuery(id+"F0.wireOp",EDGE,"E79.3.0.0")}),1.0]])]});
            var Q93;
            Q93=makeQuery(id+"F0.imprint","IMPRINT",FACE,{"disambiguationData":[TD([[makeQuery(id+"F0.imprint","IMPRINT",EDGE,{"derivedFrom":sQuery(id+"F0.wireOp",EDGE,"E79.3.0.1")}),-1.0]])]});
            var Q94;
            Q94=makeQuery(id+"F0.imprint","IMPRINT",FACE,{"disambiguationData":[TD([[makeQuery(id+"F0.imprint","IMPRINT",EDGE,{"derivedFrom":sQuery(id+"F0.wireOp",EDGE,"E79.2.0.0")}),1.0]])]});
            var Q95;
            Q95=makeQuery(id+"F0.imprint","IMPRINT",FACE,{"disambiguationData":[TD([[makeQuery(id+"F0.imprint","IMPRINT",EDGE,{"derivedFrom":sQuery(id+"F0.wireOp",EDGE,"E79.2.0.1")}),-1.0]])]});
            var Q96;
            Q96=makeQuery(id+"F0.imprint","IMPRINT",FACE,{"disambiguationData":[TD([[makeQuery(id+"F0.imprint","IMPRINT",EDGE,{"derivedFrom":sQuery(id+"F0.wireOp",EDGE,"E79.1.0.0")}),1.0]])]});
            var Q97;
            Q97=makeQuery(id+"F0.imprint","IMPRINT",FACE,{"disambiguationData":[TD([[makeQuery(id+"F0.imprint","IMPRINT",EDGE,{"derivedFrom":sQuery(id+"F0.wireOp",EDGE,"E79.1.0.1")}),-1.0]])]});
            var Q98;
            Q98=makeQuery(id+"F0.imprint","IMPRINT",FACE,{"disambiguationData":[TD([[makeQuery(id+"F0.imprint","IMPRINT",EDGE,{"derivedFrom":sQuery(id+"F0.wireOp",EDGE,"E76")}),1.0]])]});
            var Q99;
            Q99=makeQuery(id+"F0.imprint","IMPRINT",FACE,{"disambiguationData":[TD([[makeQuery(id+"F0.imprint","IMPRINT",EDGE,{"derivedFrom":sQuery(id+"F0.wireOp",EDGE,"E78.MirrorC")}),-1.0]])]});
            var Q100;
            Q100=makeQuery(id+"F0.imprint","IMPRINT",FACE,{"disambiguationData":[TD([[makeQuery(id+"F0.imprint","IMPRINT",EDGE,{"derivedFrom":sQuery(id+"F0.wireOp",EDGE,"E103")}),1.0]])]});
            var Q101;
            Q101=makeQuery(id+"F0.imprint","IMPRINT",FACE,{"disambiguationData":[TD([[makeQuery(id+"F0.imprint","IMPRINT",EDGE,{"derivedFrom":sQuery(id+"F0.wireOp",EDGE,"E104.1.0.0")}),1.0]])]});
            var Q102;
            Q102=makeQuery(id+"F0.imprint","IMPRINT",FACE,{"disambiguationData":[TD([[makeQuery(id+"F0.imprint","IMPRINT",EDGE,{"derivedFrom":sQuery(id+"F0.wireOp",EDGE,"E104.2.0.0")}),1.0]])]});
            var Q103;
            Q103=makeQuery(id+"F0.imprint","IMPRINT",FACE,{"disambiguationData":[TD([[makeQuery(id+"F0.imprint","IMPRINT",EDGE,{"derivedFrom":sQuery(id+"F0.wireOp",EDGE,"E104.3.0.0")}),1.0]])]});
            var Q104;
            Q104=makeQuery(id+"F0.imprint","IMPRINT",FACE,{"disambiguationData":[TD([[makeQuery(id+"F0.imprint","IMPRINT",EDGE,{"derivedFrom":sQuery(id+"F0.wireOp",EDGE,"E105.1.0.0")}),1.0]])]});
            var Q105;
            Q105=makeQuery(id+"F0.imprint","IMPRINT",FACE,{"disambiguationData":[TD([[makeQuery(id+"F0.imprint","IMPRINT",EDGE,{"derivedFrom":sQuery(id+"F0.wireOp",EDGE,"E105.1.0.1")}),1.0]])]});
            var Q106;
            Q106=makeQuery(id+"F0.imprint","IMPRINT",FACE,{"disambiguationData":[TD([[makeQuery(id+"F0.imprint","IMPRINT",EDGE,{"derivedFrom":sQuery(id+"F0.wireOp",EDGE,"E105.1.0.1")}),1.0]])]});
            var Q107;
            Q107=makeQuery(id+"F0.imprint","IMPRINT",FACE,{"disambiguationData":[TD([[makeQuery(id+"F0.imprint","IMPRINT",EDGE,{"derivedFrom":sQuery(id+"F0.wireOp",EDGE,"E105.1.0.2")}),1.0]])]});
            var Q108;
            Q108=makeQuery(id+"F0.imprint","IMPRINT",FACE,{"disambiguationData":[TD([[makeQuery(id+"F0.imprint","IMPRINT",EDGE,{"derivedFrom":sQuery(id+"F0.wireOp",EDGE,"E105.1.0.3")}),1.0]])]});
            var Q109;
            Q109=makeQuery(id+"F0.imprint","IMPRINT",FACE,{"disambiguationData":[TD([[makeQuery(id+"F0.imprint","IMPRINT",EDGE,{"derivedFrom":sQuery(id+"F0.wireOp",EDGE,"E105.2.0.3")}),1.0]])]});
            var Q110;
            Q110=makeQuery(id+"F0.imprint","IMPRINT",FACE,{"disambiguationData":[TD([[makeQuery(id+"F0.imprint","IMPRINT",EDGE,{"derivedFrom":sQuery(id+"F0.wireOp",EDGE,"E105.2.0.2")}),1.0]])]});
            var Q111;
            Q111=makeQuery(id+"F0.imprint","IMPRINT",FACE,{"disambiguationData":[TD([[makeQuery(id+"F0.imprint","IMPRINT",EDGE,{"derivedFrom":sQuery(id+"F0.wireOp",EDGE,"E105.3.0.0")}),1.0]])]});
            var Q112;
            Q112=makeQuery(id+"F0.imprint","IMPRINT",FACE,{"disambiguationData":[TD([[makeQuery(id+"F0.imprint","IMPRINT",EDGE,{"derivedFrom":sQuery(id+"F0.wireOp",EDGE,"E105.3.0.1")}),1.0]])]});
            var Q113;
            Q113=makeQuery(id+"F0.imprint","IMPRINT",FACE,{"disambiguationData":[TD([[makeQuery(id+"F0.imprint","IMPRINT",EDGE,{"derivedFrom":sQuery(id+"F0.wireOp",EDGE,"E105.3.0.2")}),1.0]])]});
            var Q114;
            Q114=makeQuery(id+"F0.imprint","IMPRINT",FACE,{"disambiguationData":[TD([[makeQuery(id+"F0.imprint","IMPRINT",EDGE,{"derivedFrom":sQuery(id+"F0.wireOp",EDGE,"E105.3.0.3")}),1.0]])]});
            var Q115;
            Q115=makeQuery(id+"F0.imprint","IMPRINT",FACE,{"disambiguationData":[TD([[makeQuery(id+"F0.imprint","IMPRINT",EDGE,{"derivedFrom":sQuery(id+"F0.wireOp",EDGE,"E105.2.0.1")}),1.0]])]});
            var Q116;
            Q116=makeQuery(id+"F0.imprint","IMPRINT",FACE,{"disambiguationData":[TD([[makeQuery(id+"F0.imprint","IMPRINT",EDGE,{"derivedFrom":sQuery(id+"F0.wireOp",EDGE,"E105.2.0.0")}),1.0]])]});
            var Q117;
            Q117=makeQuery(id+"F0.imprint","IMPRINT",FACE,{"disambiguationData":[TD([[makeQuery(id+"F0.imprint","IMPRINT",EDGE,{"derivedFrom":sQuery(id+"F0.wireOp",EDGE,"E105.4.0.0")}),1.0]])]});
            var Q118;
            Q118=makeQuery(id+"F0.imprint","IMPRINT",FACE,{"disambiguationData":[TD([[makeQuery(id+"F0.imprint","IMPRINT",EDGE,{"derivedFrom":sQuery(id+"F0.wireOp",EDGE,"E105.4.0.1")}),1.0]])]});
            var Q119;
            Q119=makeQuery(id+"F0.imprint","IMPRINT",FACE,{"disambiguationData":[TD([[makeQuery(id+"F0.imprint","IMPRINT",EDGE,{"derivedFrom":sQuery(id+"F0.wireOp",EDGE,"E105.4.0.2")}),1.0]])]});
            var Q120;
            Q120=makeQuery(id+"F0.imprint","IMPRINT",FACE,{"disambiguationData":[TD([[makeQuery(id+"F0.imprint","IMPRINT",EDGE,{"derivedFrom":sQuery(id+"F0.wireOp",EDGE,"E105.4.0.3")}),1.0]])]});
            var Q121;
            Q121=makeQuery(id+"F0.imprint","IMPRINT",FACE,{"disambiguationData":[TD([[makeQuery(id+"F0.imprint","IMPRINT",EDGE,{"derivedFrom":sQuery(id+"F0.wireOp",EDGE,"E105.5.0.0")}),1.0]])]});
            var Q122;
            Q122=makeQuery(id+"F0.imprint","IMPRINT",FACE,{"disambiguationData":[TD([[makeQuery(id+"F0.imprint","IMPRINT",EDGE,{"derivedFrom":sQuery(id+"F0.wireOp",EDGE,"E105.5.0.1")}),1.0]])]});
            var Q123;
            Q123=makeQuery(id+"F0.imprint","IMPRINT",FACE,{"disambiguationData":[TD([[makeQuery(id+"F0.imprint","IMPRINT",EDGE,{"derivedFrom":sQuery(id+"F0.wireOp",EDGE,"E105.5.0.2")}),1.0]])]});
            var Q124;
            Q124=makeQuery(id+"F0.imprint","IMPRINT",FACE,{"disambiguationData":[TD([[makeQuery(id+"F0.imprint","IMPRINT",EDGE,{"derivedFrom":sQuery(id+"F0.wireOp",EDGE,"E105.5.0.3")}),1.0]])]});
            var Q125;
            Q125=makeQuery(id+"F0.imprint","IMPRINT",FACE,{"disambiguationData":[TD([[makeQuery(id+"F0.imprint","IMPRINT",EDGE,{"derivedFrom":sQuery(id+"F0.wireOp",EDGE,"E101")}),1.0]])]});
            var Q126;
            Q126=makeQuery(id+"F0.imprint","IMPRINT",FACE,{"disambiguationData":[TD([[makeQuery(id+"F0.imprint","IMPRINT",EDGE,{"derivedFrom":sQuery(id+"F0.wireOp",EDGE,"E102")}),1.0]])]});
            var Q127;
            Q127=makeQuery(id+"F0.imprint","IMPRINT",FACE,{"disambiguationData":[TD([[makeQuery(id+"F0.imprint","IMPRINT",EDGE,{"derivedFrom":sQuery(id+"F0.wireOp",EDGE,"E106")}),1.0]])]});
            var Q128;
            Q128=makeQuery(id+"F0.imprint","IMPRINT",FACE,{"disambiguationData":[TD([[makeQuery(id+"F0.imprint","IMPRINT",EDGE,{"derivedFrom":sQuery(id+"F0.wireOp",EDGE,"E108")}),1.0]])]});
            var Q129;
            Q129=makeQuery(id+"F0.imprint","IMPRINT",FACE,{"disambiguationData":[TD([[makeQuery(id+"F0.imprint","IMPRINT",EDGE,{"derivedFrom":sQuery(id+"F0.wireOp",EDGE,"E112.1.0.0")}),1.0]])]});
            var Q130;
            Q130=makeQuery(id+"F0.imprint","IMPRINT",FACE,{"disambiguationData":[TD([[makeQuery(id+"F0.imprint","IMPRINT",EDGE,{"derivedFrom":sQuery(id+"F0.wireOp",EDGE,"E112.1.0.1")}),1.0]])]});
            var Q131;
            Q131=makeQuery(id+"F0.imprint","IMPRINT",FACE,{"disambiguationData":[TD([[makeQuery(id+"F0.imprint","IMPRINT",EDGE,{"derivedFrom":sQuery(id+"F0.wireOp",EDGE,"E112.1.0.2")}),1.0]])]});
            var Q132;
            Q132=makeQuery(id+"F0.imprint","IMPRINT",FACE,{"disambiguationData":[TD([[makeQuery(id+"F0.imprint","IMPRINT",EDGE,{"derivedFrom":sQuery(id+"F0.wireOp",EDGE,"E111.2.0.0")}),1.0]])]});
            var Q133;
            Q133=makeQuery(id+"F0.imprint","IMPRINT",FACE,{"disambiguationData":[TD([[makeQuery(id+"F0.imprint","IMPRINT",EDGE,{"derivedFrom":sQuery(id+"F0.wireOp",EDGE,"E111.1.0.0")}),1.0]])]});
            var Q134;
            Q134=makeQuery(id+"F0.imprint","IMPRINT",FACE,{"disambiguationData":[TD([[makeQuery(id+"F0.imprint","IMPRINT",EDGE,{"derivedFrom":sQuery(id+"F0.wireOp",EDGE,"E110")}),1.0]])]});
            extrude(context, id + "F10", {"entities" : qUnion([Q0, Q1, Q2, Q3, Q4, Q5, Q6, Q7, Q8, Q9, Q10, Q11, Q12, Q13, Q14, Q15, Q16, Q17, Q18, Q19, Q20, Q21, Q22, Q23, Q24, Q25, Q26, Q27, Q28, Q29, Q30, Q31, Q32, Q33, Q34, Q35, Q36, Q37, Q38, Q39, Q40, Q41, Q42, Q43, Q44, Q45, Q46, Q47, Q48, Q49, Q50, Q51, Q52, Q53, Q54, Q55, Q56, Q57, Q58, Q59, Q60, Q61, Q62, Q63, Q64, Q65, Q66, Q67, Q68, Q69, Q70, Q71, Q72, Q73, Q74, Q75, Q76, Q77, Q78, Q79, Q80, Q81, Q82, Q83, Q84, Q85, Q86, Q87, Q88, Q89, Q90, Q91, Q92, Q93, Q94, Q95, Q96, Q97, Q98, Q99, Q100, Q101, Q102, Q103, Q104, Q105, Q106, Q107, Q108, Q109, Q110, Q111, Q112, Q113, Q114, Q115, Q116, Q117, Q118, Q119, Q120, Q121, Q122, Q123, Q124, Q125, Q126, Q127, Q128, Q129, Q130, Q131, Q132, Q133, Q134]), "operationType" : NewBodyOperationType.ADD, "depth" : 10 * mm, "hasSecondDirection" : true, "secondDirectionOppositeDirection" : true, "secondDirectionDepth" : 1 * mm});
        }
        {
            var Q0;
            Q0=makeQuery(id+"F2.opExtrude","CAP_FACE",FACE,{"disambiguationData":[OSD([sQuery(id+"F0.wireOp",EDGE,"E0"),sQuery(id+"F0.wireOp",EDGE,"E1"),sQuery(id+"F0.wireOp",EDGE,"E2"),sQuery(id+"F0.wireOp",EDGE,"E3.bottom"),sQuery(id+"F0.wireOp",EDGE,"E3.top"),sQuery(id+"F0.wireOp",EDGE,"E3.left"),sQuery(id+"F0.wireOp",EDGE,"E3.right"),sQuery(id+"F0.wireOp",EDGE,"E4.1.0.0"),sQuery(id+"F0.wireOp",EDGE,"E4.1.0.1"),sQuery(id+"F0.wireOp",EDGE,"E4.1.0.2"),sQuery(id+"F0.wireOp",EDGE,"E4.1.0.3"),sQuery(id+"F0.wireOp",EDGE,"E4.2.0.0"),sQuery(id+"F0.wireOp",EDGE,"E4.2.0.1"),sQuery(id+"F0.wireOp",EDGE,"E4.2.0.2"),sQuery(id+"F0.wireOp",EDGE,"E4.2.0.3"),sQuery(id+"F0.wireOp",EDGE,"E4.3.0.0"),sQuery(id+"F0.wireOp",EDGE,"E4.3.0.1"),sQuery(id+"F0.wireOp",EDGE,"E4.3.0.2"),sQuery(id+"F0.wireOp",EDGE,"E4.3.0.3"),sQuery(id+"F0.wireOp",EDGE,"E4.4.0.0"),sQuery(id+"F0.wireOp",EDGE,"E4.4.0.1"),sQuery(id+"F0.wireOp",EDGE,"E4.4.0.2"),sQuery(id+"F0.wireOp",EDGE,"E4.4.0.3"),sQuery(id+"F0.wireOp",EDGE,"E5"),sQuery(id+"F0.wireOp",EDGE,"E6"),sQuery(id+"F0.wireOp",EDGE,"E7"),sQuery(id+"F0.wireOp",EDGE,"E8"),sQuery(id+"F0.wireOp",EDGE,"E9.bottom"),sQuery(id+"F0.wireOp",EDGE,"E9.top"),sQuery(id+"F0.wireOp",EDGE,"E9.left"),sQuery(id+"F0.wireOp",EDGE,"E9.right"),sQuery(id+"F0.wireOp",EDGE,"E10.1.0.0"),sQuery(id+"F0.wireOp",EDGE,"E10.1.0.1"),sQuery(id+"F0.wireOp",EDGE,"E10.1.0.2"),sQuery(id+"F0.wireOp",EDGE,"E10.1.0.3"),sQuery(id+"F0.wireOp",EDGE,"E10.2.0.0"),sQuery(id+"F0.wireOp",EDGE,"E10.2.0.1"),sQuery(id+"F0.wireOp",EDGE,"E10.2.0.2"),sQuery(id+"F0.wireOp",EDGE,"E10.2.0.3"),sQuery(id+"F0.wireOp",EDGE,"E11.bottom"),sQuery(id+"F0.wireOp",EDGE,"E11.top"),sQuery(id+"F0.wireOp",EDGE,"E11.left"),sQuery(id+"F0.wireOp",EDGE,"E11.right"),sQuery(id+"F0.wireOp",EDGE,"E12.bottom"),sQuery(id+"F0.wireOp",EDGE,"E12.top"),sQuery(id+"F0.wireOp",EDGE,"E12.left"),sQuery(id+"F0.wireOp",EDGE,"E12.right"),sQuery(id+"F0.wireOp",EDGE,"E13.bottom"),sQuery(id+"F0.wireOp",EDGE,"E13.top"),sQuery(id+"F0.wireOp",EDGE,"E13.left"),sQuery(id+"F0.wireOp",EDGE,"E13.right"),sQuery(id+"F0.wireOp",EDGE,"E14.bottom"),sQuery(id+"F0.wireOp",EDGE,"E14.top"),sQuery(id+"F0.wireOp",EDGE,"E14.left"),sQuery(id+"F0.wireOp",EDGE,"E14.right"),sQuery(id+"F0.wireOp",EDGE,"E15.bottom"),sQuery(id+"F0.wireOp",EDGE,"E15.top"),sQuery(id+"F0.wireOp",EDGE,"E15.left"),sQuery(id+"F0.wireOp",EDGE,"E15.right"),sQuery(id+"F0.wireOp",EDGE,"E16.bottom"),sQuery(id+"F0.wireOp",EDGE,"E16.top"),sQuery(id+"F0.wireOp",EDGE,"E16.left"),sQuery(id+"F0.wireOp",EDGE,"E16.right"),sQuery(id+"F0.wireOp",EDGE,"E17.bottom"),sQuery(id+"F0.wireOp",EDGE,"E17.top"),sQuery(id+"F0.wireOp",EDGE,"E17.left"),sQuery(id+"F0.wireOp",EDGE,"E17.right"),sQuery(id+"F0.wireOp",EDGE,"E18.bottom"),sQuery(id+"F0.wireOp",EDGE,"E18.top"),sQuery(id+"F0.wireOp",EDGE,"E18.left"),sQuery(id+"F0.wireOp",EDGE,"E18.right"),sQuery(id+"F0.wireOp",EDGE,"E19.bottom"),sQuery(id+"F0.wireOp",EDGE,"E19.top"),sQuery(id+"F0.wireOp",EDGE,"E19.left"),sQuery(id+"F0.wireOp",EDGE,"E19.right"),sQuery(id+"F0.wireOp",EDGE,"E20.bottom"),sQuery(id+"F0.wireOp",EDGE,"E20.top"),sQuery(id+"F0.wireOp",EDGE,"E20.left"),sQuery(id+"F0.wireOp",EDGE,"E20.right"),sQuery(id+"F0.wireOp",EDGE,"E21.bottom"),sQuery(id+"F0.wireOp",EDGE,"E21.top"),sQuery(id+"F0.wireOp",EDGE,"E21.right"),sQuery(id+"F0.wireOp",EDGE,"E22"),sQuery(id+"F0.wireOp",EDGE,"E23"),sQuery(id+"F0.wireOp",EDGE,"E24.bottom"),sQuery(id+"F0.wireOp",EDGE,"E24.top"),sQuery(id+"F0.wireOp",EDGE,"E24.left"),sQuery(id+"F0.wireOp",EDGE,"E24.right"),sQuery(id+"F0.wireOp",EDGE,"E25.bottom"),sQuery(id+"F0.wireOp",EDGE,"E25.top"),sQuery(id+"F0.wireOp",EDGE,"E25.left"),sQuery(id+"F0.wireOp",EDGE,"E25.right"),sQuery(id+"F0.wireOp",EDGE,"E26.1.0.0"),sQuery(id+"F0.wireOp",EDGE,"E26.1.0.1"),sQuery(id+"F0.wireOp",EDGE,"E26.1.0.2"),sQuery(id+"F0.wireOp",EDGE,"E26.1.0.3"),sQuery(id+"F0.wireOp",EDGE,"E26.2.0.0"),sQuery(id+"F0.wireOp",EDGE,"E26.2.0.1"),sQuery(id+"F0.wireOp",EDGE,"E26.2.0.2"),sQuery(id+"F0.wireOp",EDGE,"E26.2.0.3"),sQuery(id+"F0.wireOp",EDGE,"E26.3.0.0"),sQuery(id+"F0.wireOp",EDGE,"E26.3.0.1"),sQuery(id+"F0.wireOp",EDGE,"E26.3.0.2"),sQuery(id+"F0.wireOp",EDGE,"E26.3.0.3"),sQuery(id+"F0.wireOp",EDGE,"E26.4.0.0"),sQuery(id+"F0.wireOp",EDGE,"E26.4.0.1"),sQuery(id+"F0.wireOp",EDGE,"E26.4.0.2"),sQuery(id+"F0.wireOp",EDGE,"E26.4.0.3"),sQuery(id+"F0.wireOp",EDGE,"E26.5.0.0"),sQuery(id+"F0.wireOp",EDGE,"E26.5.0.1"),sQuery(id+"F0.wireOp",EDGE,"E26.5.0.2"),sQuery(id+"F0.wireOp",EDGE,"E26.5.0.3"),sQuery(id+"F0.wireOp",EDGE,"E27.bottom"),sQuery(id+"F0.wireOp",EDGE,"E27.top"),sQuery(id+"F0.wireOp",EDGE,"E27.left"),sQuery(id+"F0.wireOp",EDGE,"E27.right"),sQuery(id+"F0.wireOp",EDGE,"E28.bottom"),sQuery(id+"F0.wireOp",EDGE,"E28.top"),sQuery(id+"F0.wireOp",EDGE,"E28.left"),sQuery(id+"F0.wireOp",EDGE,"E28.right"),sQuery(id+"F0.wireOp",EDGE,"E29.1.0.0"),sQuery(id+"F0.wireOp",EDGE,"E29.1.0.1"),sQuery(id+"F0.wireOp",EDGE,"E29.1.0.2"),sQuery(id+"F0.wireOp",EDGE,"E29.1.0.3"),sQuery(id+"F0.wireOp",EDGE,"E29.1.0.4"),sQuery(id+"F0.wireOp",EDGE,"E29.1.0.5"),sQuery(id+"F0.wireOp",EDGE,"E29.1.0.6"),sQuery(id+"F0.wireOp",EDGE,"E29.1.0.7"),sQuery(id+"F0.wireOp",EDGE,"E29.2.0.0"),sQuery(id+"F0.wireOp",EDGE,"E29.2.0.1"),sQuery(id+"F0.wireOp",EDGE,"E29.2.0.2"),sQuery(id+"F0.wireOp",EDGE,"E29.2.0.3"),sQuery(id+"F0.wireOp",EDGE,"E29.2.0.4"),sQuery(id+"F0.wireOp",EDGE,"E29.2.0.5"),sQuery(id+"F0.wireOp",EDGE,"E29.2.0.6"),sQuery(id+"F0.wireOp",EDGE,"E29.2.0.7"),sQuery(id+"F0.wireOp",EDGE,"E29.3.0.0"),sQuery(id+"F0.wireOp",EDGE,"E29.3.0.1"),sQuery(id+"F0.wireOp",EDGE,"E29.3.0.2"),sQuery(id+"F0.wireOp",EDGE,"E29.3.0.3"),sQuery(id+"F0.wireOp",EDGE,"E29.3.0.4"),sQuery(id+"F0.wireOp",EDGE,"E29.3.0.5"),sQuery(id+"F0.wireOp",EDGE,"E29.3.0.6"),sQuery(id+"F0.wireOp",EDGE,"E29.3.0.7"),sQuery(id+"F0.wireOp",EDGE,"E29.4.0.0"),sQuery(id+"F0.wireOp",EDGE,"E29.4.0.1"),sQuery(id+"F0.wireOp",EDGE,"E29.4.0.2"),sQuery(id+"F0.wireOp",EDGE,"E29.4.0.3"),sQuery(id+"F0.wireOp",EDGE,"E29.4.0.4"),sQuery(id+"F0.wireOp",EDGE,"E29.4.0.5"),sQuery(id+"F0.wireOp",EDGE,"E29.4.0.6"),sQuery(id+"F0.wireOp",EDGE,"E29.4.0.7"),sQuery(id+"F0.wireOp",EDGE,"E29.5.0.0"),sQuery(id+"F0.wireOp",EDGE,"E29.5.0.1"),sQuery(id+"F0.wireOp",EDGE,"E29.5.0.2"),sQuery(id+"F0.wireOp",EDGE,"E29.5.0.3"),sQuery(id+"F0.wireOp",EDGE,"E29.5.0.4"),sQuery(id+"F0.wireOp",EDGE,"E29.5.0.5"),sQuery(id+"F0.wireOp",EDGE,"E29.5.0.6"),sQuery(id+"F0.wireOp",EDGE,"E29.5.0.7"),sQuery(id+"F0.wireOp",EDGE,"E30.bottom"),sQuery(id+"F0.wireOp",EDGE,"E30.top"),sQuery(id+"F0.wireOp",EDGE,"E30.left"),sQuery(id+"F0.wireOp",EDGE,"E30.right"),sQuery(id+"F0.wireOp",EDGE,"E31.bottom"),sQuery(id+"F0.wireOp",EDGE,"E31.top"),sQuery(id+"F0.wireOp",EDGE,"E31.left"),sQuery(id+"F0.wireOp",EDGE,"E31.right"),sQuery(id+"F0.wireOp",EDGE,"E32.1.0.0"),sQuery(id+"F0.wireOp",EDGE,"E32.1.0.1"),sQuery(id+"F0.wireOp",EDGE,"E32.1.0.2"),sQuery(id+"F0.wireOp",EDGE,"E32.1.0.3"),sQuery(id+"F0.wireOp",EDGE,"E32.2.0.0"),sQuery(id+"F0.wireOp",EDGE,"E32.2.0.1"),sQuery(id+"F0.wireOp",EDGE,"E32.2.0.2"),sQuery(id+"F0.wireOp",EDGE,"E32.2.0.3"),sQuery(id+"F0.wireOp",EDGE,"E32.3.0.0"),sQuery(id+"F0.wireOp",EDGE,"E32.3.0.1"),sQuery(id+"F0.wireOp",EDGE,"E32.3.0.2"),sQuery(id+"F0.wireOp",EDGE,"E32.3.0.3"),sQuery(id+"F0.wireOp",EDGE,"E32.4.0.0"),sQuery(id+"F0.wireOp",EDGE,"E32.4.0.1"),sQuery(id+"F0.wireOp",EDGE,"E32.4.0.2"),sQuery(id+"F0.wireOp",EDGE,"E32.4.0.3"),sQuery(id+"F0.wireOp",EDGE,"E32.5.0.0"),sQuery(id+"F0.wireOp",EDGE,"E32.5.0.1"),sQuery(id+"F0.wireOp",EDGE,"E32.5.0.2"),sQuery(id+"F0.wireOp",EDGE,"E32.5.0.3"),sQuery(id+"F0.wireOp",EDGE,"E34"),sQuery(id+"F0.wireOp",EDGE,"E35"),sQuery(id+"F0.wireOp",EDGE,"E36"),sQuery(id+"F0.wireOp",EDGE,"E37"),sQuery(id+"F0.wireOp",EDGE,"E41.bottom"),sQuery(id+"F0.wireOp",EDGE,"E41.top"),sQuery(id+"F0.wireOp",EDGE,"E41.left"),sQuery(id+"F0.wireOp",EDGE,"E41.right"),sQuery(id+"F0.wireOp",EDGE,"E109.bottom"),sQuery(id+"F0.wireOp",EDGE,"E109.top"),sQuery(id+"F0.wireOp",EDGE,"E109.left"),sQuery(id+"F0.wireOp",EDGE,"E109.right")])],"isStart":true});
            var sketch = newSketch(context, id + "F11", { "sketchPlane" : qUnion([Q0])});
            skLineSegment(sketch, "E122.bottom", {"start": v(90.58, 1.52) * mm, "end": v(96.25, 1.52) * mm});
            skLineSegment(sketch, "E122.top", {"start": v(90.58, -41.78) * mm, "end": v(96.25, -41.78) * mm});
            skLineSegment(sketch, "E122.left", {"start": v(87.08, -1.98) * mm, "end": v(87.08, -38.28) * mm});
            skLineSegment(sketch, "E122.right", {"start": v(138, -18.52) * mm, "end": v(138, -21.74) * mm});
            skCircle(sketch, "E123.0", {"center": v(90.39, -2.13) * mm, "radius": 1.95 * mm});
            skCircle(sketch, "E123.1", {"center": v(90.39, -37.15) * mm, "radius": 1.95 * mm});
            skPoint(sketch, "E124.visualSharp", {"position": v(87.08, 1.52) * mm});
            skArc(sketch, "E124.filletArc", {"start": v(90.58, 1.52) * mm, "mid": v(88.1, 0.5) * mm, "end": v(87.08, -1.98) * mm});
            skPoint(sketch, "E125.visualSharp", {"position": v(87.08, -41.78) * mm});
            skArc(sketch, "E125.filletArc", {"start": v(87.08, -38.28) * mm, "mid": v(88.1, -40.76) * mm, "end": v(90.58, -41.78) * mm});
            skLineSegment(sketch, "E126", {"start": v(87.08, -20.13) * mm, "end": v(114.03, -20.13) * mm, "construction": true});
            skLineSegment(sketch, "E127", {"start": v(96.25, 1.52) * mm, "end": v(99.09, -9.75) * mm});
            skLineSegment(sketch, "E128", {"start": v(103.93, -13.52) * mm, "end": v(133, -13.52) * mm});
            skLineSegment(sketch, "E129.MirrorCS", {"start": v(103.93, -26.74) * mm, "end": v(133, -26.74) * mm});
            skLineSegment(sketch, "E130.MirrorCS", {"start": v(96.25, -41.78) * mm, "end": v(99.09, -30.52) * mm});
            skArc(sketch, "E131", {"start": v(114.03, -18.13) * mm, "mid": v(112.03, -20.13) * mm, "end": v(114.03, -22.13) * mm});
            skArc(sketch, "E132", {"start": v(130.3, -22.13) * mm, "mid": v(132.3, -20.13) * mm, "end": v(130.3, -18.13) * mm});
            skLineSegment(sketch, "E133", {"start": v(114.03, -20.13) * mm, "end": v(130.3, -20.13) * mm, "construction": true});
            skLineSegment(sketch, "E134", {"start": v(114.03, -18.13) * mm, "end": v(130.3, -18.13) * mm});
            skLineSegment(sketch, "E135", {"start": v(114.03, -22.13) * mm, "end": v(130.3, -22.13) * mm});
            skPoint(sketch, "E136.visualSharp", {"position": v(138, -13.52) * mm});
            skArc(sketch, "E136.filletArc", {"start": v(138, -18.52) * mm, "mid": v(136.53, -14.99) * mm, "end": v(133, -13.52) * mm});
            skPoint(sketch, "E137.visualSharp", {"position": v(138, -26.74) * mm});
            skArc(sketch, "E137.filletArc", {"start": v(133, -26.74) * mm, "mid": v(136.53, -25.28) * mm, "end": v(138, -21.74) * mm});
            skPoint(sketch, "E138.visualSharp", {"position": v(100.04, -13.52) * mm});
            skArc(sketch, "E138.filletArc", {"start": v(99.09, -9.75) * mm, "mid": v(100.86, -12.47) * mm, "end": v(103.93, -13.52) * mm});
            skPoint(sketch, "E139.visualSharp", {"position": v(100.04, -26.74) * mm});
            skArc(sketch, "E139.filletArc", {"start": v(103.93, -26.74) * mm, "mid": v(100.86, -27.8) * mm, "end": v(99.09, -30.52) * mm});
            skSolve(sketch);
        }
        {
            var Q0;
            {var subQ0=sQuery(id+"F11.wireOp",EDGE,"E122.right");Q0=makeQuery(id+"F11.imprint","IMPRINT",FACE,{"disambiguationData":[TD([[makeQuery(id+"F11.imprint","IMPRINT",EDGE,{"derivedFrom":subQ0}),-1.0]])]});}
            var Q1;
            Q1=makeQuery(id+"F11.imprint","IMPRINT",FACE,{"disambiguationData":[TD([[makeQuery(id+"F11.imprint","IMPRINT",EDGE,{"derivedFrom":sQuery(id+"F11.wireOp",EDGE,"E122.left")}),1.0]])]});
            extrude(context, id + "F12", {"entities" : qUnion([Q0, Q1]), "depth" : 1.5 * mm});
        }
        {
            var Q0;
            Q0=makeQuery(id+"F12.opExtrude","CAP_EDGE",EDGE,{"disambiguationData":[OSD([sQuery(id+"F11.wireOp",EDGE,"E123.0")])],"isStart":false});
            var Q1;
            Q1=makeQuery(id+"F12.opExtrude","CAP_EDGE",EDGE,{"disambiguationData":[OSD([sQuery(id+"F11.wireOp",EDGE,"E123.1")])],"isStart":false});
            var Q2;
            Q2=makeQuery(id+"F12.opExtrude","CAP_EDGE",EDGE,{"disambiguationData":[OSD([sQuery(id+"F11.wireOp",EDGE,"E132")])],"isStart":false});
            chamfer(context, id + "F13", {"entities" : qUnion([Q0, Q1, Q2]), "width" : .5 * mm, "tangentPropagation" : true});
        }
        {
            var Q0;
            Q0=makeQuery(id+"F12.opExtrude","CAP_FACE",FACE,{"disambiguationData":[OSD([sQuery(id+"F11.wireOp",EDGE,"E122.bottom"),sQuery(id+"F11.wireOp",EDGE,"E122.top"),sQuery(id+"F11.wireOp",EDGE,"E122.left"),sQuery(id+"F11.wireOp",EDGE,"E122.right"),sQuery(id+"F11.wireOp",EDGE,"E123.0"),sQuery(id+"F11.wireOp",EDGE,"E123.1"),sQuery(id+"F11.wireOp",EDGE,"E124.filletArc"),sQuery(id+"F11.wireOp",EDGE,"E125.filletArc"),sQuery(id+"F11.wireOp",EDGE,"E127"),sQuery(id+"F11.wireOp",EDGE,"E128"),sQuery(id+"F11.wireOp",EDGE,"E129.MirrorCS"),sQuery(id+"F11.wireOp",EDGE,"E130.MirrorCS"),sQuery(id+"F11.wireOp",EDGE,"E131"),sQuery(id+"F11.wireOp",EDGE,"E132"),sQuery(id+"F11.wireOp",EDGE,"E134"),sQuery(id+"F11.wireOp",EDGE,"E135")])],"isStart":false});
            fillet(context, id + "F14", {"entities" : qUnion([Q0]), "radius" : .25 * mm, "tangentPropagation" : true, "allowEdgeOverflow" : false});
        }
    });
